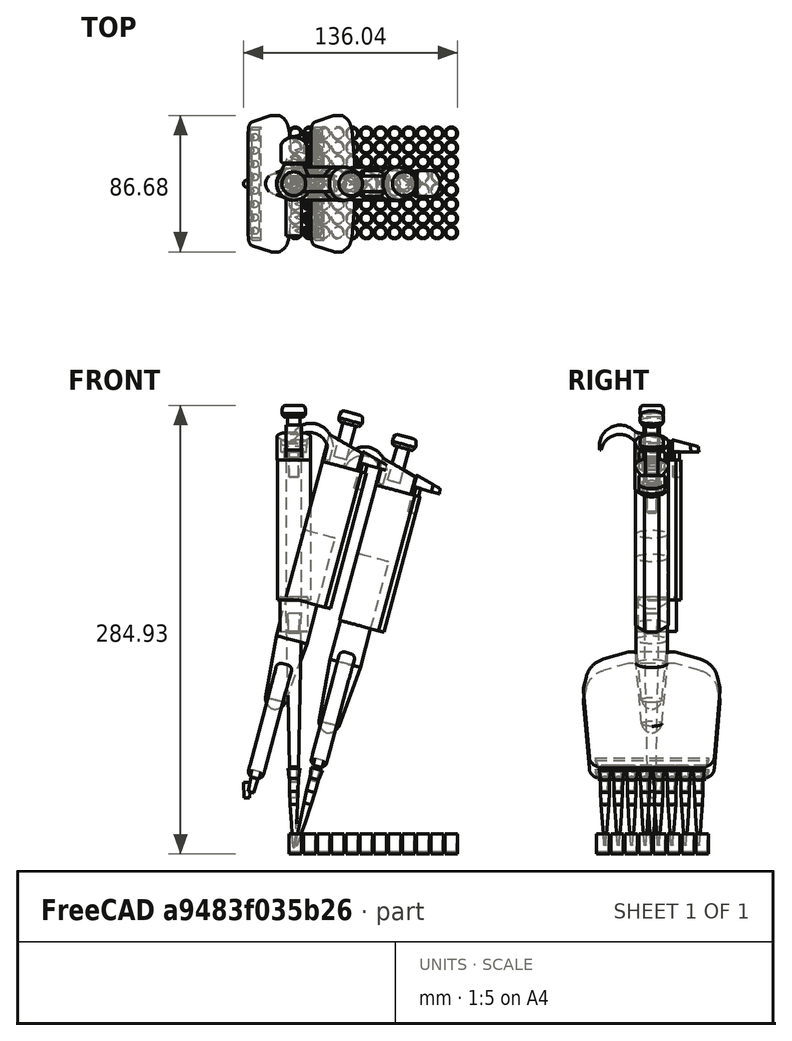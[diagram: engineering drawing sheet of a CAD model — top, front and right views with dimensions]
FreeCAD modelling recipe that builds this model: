
FCSTD DOCUMENT  (FreeCAD 0.20R29410 (Git))
Label: Pipettes
License: All rights reserved
LicenseURL: http://en.wikipedia.org/wiki/All_rights_reserved
objects: Sketcher::SketchObject×37, PartDesign::Body×30, PartDesign::Pad×14, Part::Compound×13, PartDesign::Revolution×9, Part::FeaturePython×7, PartDesign::AdditiveLoft×7, TechDraw::DrawViewPart×7, PartDesign::ShapeBinder×6, PartDesign::Plane×6, Part::Thickness×3, Image::ImagePlane×2, Part::Fillet×2, TechDraw::DrawSVGTemplate×2, TechDraw::DrawPage×2, Part::Cylinder×1, Part::Cut×1, App::Part×1
note: 160 computed .brp shape members not serialized (recipe doc carries the construction recipe); baked Part::Feature solids carry a one-line shape summary decoded from their .brp

FEATURE [Image::ImagePlane] ImagePlane
  Placement = pos=(-11,0,28) rot=(-1,0,0;4.71239rad)
  XSize = 251.23
  YSize = 373.42
FEATURE [Part::Thickness] Thickness001  label="2-200 tip"
  Intersection = false
  Join = 0
  Mode = 0
  Placement = pos=(0,0,-137) rot=(0,0,1;0rad)
  SelfIntersection = false
  Value = 0.1
FEATURE [Part::FeaturePython] Array  label="Array of tips"  # Draft array (typed FeaturePython)
  AlwaysSyncPlacement = false
  Angle = 360
  ArrayType = 0
  Axis = (0,0,1)
  Base = -> Thickness001
  Center = (0,0,0)
  Count = 8
  ExpandArray = false
  Fuse = false
  IntervalAxis = (0,0,0)
  IntervalX = (8.5,0,0)
  IntervalY = (0,100,0)
  IntervalZ = (0,0,100)
  NumberCircles = 3
  NumberPolar = 5
  NumberX = 8
  NumberY = 1
  NumberZ = 1
  Placement = pos=(-29.75,0,-11) rot=(0,0,1;0rad)
  PlacementList = 8 placements: arithmetic series from (0,0,-137) step (8.5,0,0) to (59.5,0,-137)
  RadialDistance = 50
  ScaleList = (8) [(1,1,1),(1,1,1),(1,1,1),(1,1,1),(1,1,1),(1,1,1),(1,1,1),(1,1,1)]
  Symmetry = 1
  TangentialDistance = 25
FEATURE [Sketcher::SketchObject] Sketch
  FullyConstrained = false
  MapMode = 5
  Placement = pos=(0,0,0) rot=(1,0,0;1.5708rad)
  Support = -> [XZ_Plane]
  sketch-geometry (18):
    g0: LineSegment StartX=39.7221 StartY=-89.5995 StartZ=0 EndX=43.3704 EndY=-45.7141 EndZ=0
    g1: LineSegment StartX=43.3704 StartY=-45.7141 StartZ=0 EndX=41.5984 EndY=-37.853 EndZ=0
    g2: LineSegment StartX=30.7067 StartY=-26.3243 StartZ=0 EndX=14.3773 EndY=-21.6547 EndZ=0
    g3: LineSegment StartX=-14.3773 StartY=-21.6547 StartZ=0 EndX=-30.7067 EndY=-26.3243 EndZ=0
    g4: LineSegment StartX=-41.5984 StartY=-37.853 StartZ=0 EndX=-43.3704 EndY=-45.7141 EndZ=0
    g5: LineSegment StartX=-43.3704 StartY=-45.7141 StartZ=0 EndX=-39.7221 EndY=-89.5995 EndZ=0
    g6: LineSegment StartX=-14.3773 StartY=-21.6547 StartZ=0 EndX=0 EndY=-21.6547 EndZ=0
    g7: LineSegment StartX=14.3773 StartY=-21.6547 StartZ=0 EndX=0 EndY=-21.6547 EndZ=0
    g8: LineSegment StartX=33.0605 StartY=-95.7303 StartZ=0 EndX=0 EndY=-95.7303 EndZ=0
    g9: LineSegment StartX=0 StartY=-95.7303 StartZ=0 EndX=-33.0605 EndY=-95.7303 EndZ=0
    g10: LineSegment StartX=43.3704 StartY=-45.7141 StartZ=0 EndX=-43.3704 EndY=-45.7141 EndZ=0
    g11: ArcOfCircle CenterX=26.4323 CenterY=-41.2717 CenterZ=0 NormalX=0 NormalY=0 NormalZ=1 AngleXU=0 Radius=15.5465 StartAngle=0.221711 EndAngle=1.29227
    g12: ArcOfCircle CenterX=-26.4323 CenterY=-41.2717 CenterZ=0 NormalX=0 NormalY=0 NormalZ=1 AngleXU=0 Radius=15.5465 StartAngle=1.84932 EndAngle=2.91988
    g13: LineSegment StartX=41.5984 StartY=-37.853 StartZ=0 EndX=-41.5984 EndY=-37.853 EndZ=0
    g14: LineSegment StartX=-30.7067 StartY=-26.3243 StartZ=0 EndX=30.7067 EndY=-26.3243 EndZ=0
    g15: ArcOfCircle CenterX=33.0605 CenterY=-89.0457 CenterZ=0 NormalX=0 NormalY=0 NormalZ=1 AngleXU=0 Radius=6.6846 StartAngle=4.71239 EndAngle=6.20025
    g16: ArcOfCircle CenterX=-33.0605 CenterY=-89.0457 CenterZ=0 NormalX=0 NormalY=0 NormalZ=1 AngleXU=0 Radius=6.6846 StartAngle=3.22453 EndAngle=4.71239
    g17: LineSegment StartX=39.7221 StartY=-89.5995 StartZ=0 EndX=-39.7221 EndY=-89.5995 EndZ=0
  constraints (36):
    c: Coincident(g1,g0)
    c: Coincident(g5,g4)
    c: Coincident(g6,g3)
    c: PointOnObject(g6,g-2)
    c: Horizontal(g6)
    c: Coincident(g7,g2)
    c: Coincident(g7,g6)
    c: Horizontal(g7)
    c: PointOnObject(g8,g-2)
    c: Horizontal(g8)
    c: Coincident(g9,g8)
    c: Horizontal(g9)
    c: Equal(g0,g5)
    c: Equal(g1,g4)
    c: Equal(g3,g2)
    c: Equal(g7,g6)
    c: Equal(g8,g9)
    c: Coincident(g10,g0)
    c: Coincident(g10,g4)
    c: Horizontal(g10)
    c: Tangent(g2,g11) = -1.5708
    c: Tangent(g1,g11) = -1.5708
    c: Tangent(g3,g12) = -1.5708
    c: Tangent(g4,g12) = -1.5708
    c: Coincident(g13,g1)
    c: Coincident(g13,g4)
    c: Horizontal(g13)
    c: Coincident(g14,g3)
    c: Coincident(g14,g2)
    c: Horizontal(g14)
    c: Tangent(g0,g15) = -1.5708
    c: Tangent(g8,g15) = 1.5708
    c: Tangent(g9,g16) = 1.5708
    c: Tangent(g5,g16) = -1.5708
    c: Coincident(g17,g0)
    c: Coincident(g17,g5)
FEATURE [PartDesign::Pad] Pad
  Direction = (0,-1,2e-16)
  Length = 10
  Length2 = 10
  Midplane = true
  Placement = pos=(0,0,0) rot=(1,0,0;1.5708rad)
  Profile = -> Sketch
  ReferenceAxis = -> Sketch [N_Axis]
  Type = 0
FEATURE [PartDesign::Body] Body
  Group = -> [Sketch,Pad]
  Origin = -> Origin
  Tip = -> Pad
FEATURE [Part::Fillet] Fillet  label="Main body"
  Base = -> Body
  Edges = 32 edges r=3: [Edge3,Edge4,Edge5,Edge6,Edge7,Edge9,Edge10,Edge12,Edge13,Edge14,Edge15,Edge16,Edge18,Edge19,Edge20,Edge21,Edge22,Edge24,Edge25,Edge27,Edge28,Edge29,Edge30,Edge31,Edge33,Edge34,Edge36,Edge37,Edge39,Edge40,Edge41,Edge42]
FEATURE [Sketcher::SketchObject] Sketch001
  FullyConstrained = false
  MapMode = 5
  Placement = pos=(0,0,0) rot=(1,0,0;1.5708rad)
  Support = -> [XZ_Plane001]
  sketch-geometry (6):
    g0: LineSegment StartX=0 StartY=-83.0877 StartZ=0 EndX=6.48261 EndY=-83.0877 EndZ=0
    g1: ArcOfCircle CenterX=-0.717331 CenterY=-81.8107 CenterZ=0 NormalX=0 NormalY=0 NormalZ=1 AngleXU=0 Radius=7.31232 StartAngle=4.81065 EndAngle=6.10764
    g2: LineSegment StartX=6.48261 StartY=-83.0877 StartZ=0 EndX=10 EndY=-43.4831 EndZ=0
    g3: LineSegment StartX=10 StartY=-43.4831 StartZ=0 EndX=10 EndY=25.9449 EndZ=0
    g4: LineSegment StartX=10 StartY=25.9449 StartZ=0 EndX=0 EndY=25.9449 EndZ=0
    g5: LineSegment StartX=0 StartY=25.9449 StartZ=0 EndX=0 EndY=-89.0877 EndZ=0
  constraints (14):
    c: PointOnObject(g0,g-2)
    c: Horizontal(g0)
    c: Coincident(g1,g0)
    c: Coincident(g2,g1)
    c: Coincident(g3,g2)
    c: Vertical(g3)
    c: Coincident(g4,g3)
    c: PointOnObject(g4,g-2)
    c: Horizontal(g4)
    c: Coincident(g5,g4)
    c: Coincident(g5,g1)
    c: Vertical(g5)
    c: DistanceY(g1,g0) = 6
    c: DistanceX(g4,g4) = 10
FEATURE [PartDesign::Revolution] Revolution
  Angle = 360
  Axis = (0,2e-16,1)
  Base = (0,0,0)
  Placement = pos=(0,0,0) rot=(1,0,0;1.5708rad)
  Profile = -> Sketch001
  ReferenceAxis = -> Sketch001 [V_Axis]
  Reversed = true
FEATURE [PartDesign::Body] Body001
  Group = -> [Sketch001,Revolution]
  Origin = -> Origin001
  Placement = pos=(0,0,38) rot=(0,0,1;0rad)
  Tip = -> Revolution
FEATURE [Sketcher::SketchObject] Sketch002
  AttachmentOffset = pos=(0,0,30) rot=(0,0,1;0rad)
  FullyConstrained = false
  MapMode = 5
  Placement = pos=(0,0,30) rot=(0,0,1;0rad)
  Support = -> [XY_Plane002]
  sketch-geometry (6):
    g0: ArcOfCircle CenterX=0 CenterY=0 CenterZ=0 NormalX=0 NormalY=0 NormalZ=1 AngleXU=0 Radius=10.5222 StartAngle=1.15093 EndAngle=5.13225
    g1: ArcOfCircle CenterX=13.606 CenterY=0 CenterZ=0 NormalX=0 NormalY=0 NormalZ=1 AngleXU=0 Radius=4.99301 StartAngle=5.04934 EndAngle=7.51703
    g2: LineSegment StartX=4.28922 StartY=-9.60826 StartZ=0 EndX=4.28922 EndY=9.60826 EndZ=0
    g3: LineSegment StartX=15.2568 StartY=4.71224 StartZ=0 EndX=4.28922 EndY=9.60826 EndZ=0
    g4: LineSegment StartX=15.2568 StartY=-4.71224 StartZ=0 EndX=4.28922 EndY=-9.60826 EndZ=0
    g5: LineSegment StartX=15.2568 StartY=-4.71224 StartZ=0 EndX=15.2568 EndY=4.71224 EndZ=0
  constraints (12):
    c: Coincident(g0,g-1)
    c: PointOnObject(g1,g-1)
    c: Coincident(g2,g0)
    c: Coincident(g2,g0)
    c: Vertical(g2)
    c: Coincident(g3,g1)
    c: Coincident(g3,g0)
    c: Coincident(g4,g1)
    c: Coincident(g4,g0)
    c: Coincident(g5,g1)
    c: Coincident(g5,g1)
    c: Vertical(g5)
FEATURE [PartDesign::Pad] Pad001
  Direction = (0,0,1)
  Length = 89
  Length2 = 10
  Profile = -> Sketch002
  ReferenceAxis = -> Sketch002 [N_Axis]
  Type = 0
FEATURE [PartDesign::Body] Body002  label="Handle down"
  Group = -> [Sketch002,Pad001]
  Origin = -> Origin002
  Placement = pos=(0,0,-10) rot=(0,0,1;0rad)
  Tip = -> Pad001
FEATURE [Sketcher::SketchObject] Sketch003
  FullyConstrained = false
  MapMode = 5
  Placement = pos=(0,0,0) rot=(1,0,0;1.5708rad)
  Support = -> [XZ_Plane003]
  sketch-geometry (6):
    g0: LineSegment StartX=0 StartY=-91.478 StartZ=0 EndX=35.9271 EndY=-91.478 EndZ=0
    g1: LineSegment StartX=35.9271 StartY=-91.478 StartZ=0 EndX=34.2632 EndY=-96.4699 EndZ=0
    g2: LineSegment StartX=34.2632 StartY=-96.4699 StartZ=0 EndX=0 EndY=-96.4699 EndZ=0
    g3: LineSegment StartX=0 StartY=-96.4699 StartZ=0 EndX=-34.2632 EndY=-96.4699 EndZ=0
    g4: LineSegment StartX=-34.2632 StartY=-96.4699 StartZ=0 EndX=-35.9271 EndY=-91.478 EndZ=0
    g5: LineSegment StartX=-35.9271 StartY=-91.478 StartZ=0 EndX=0 EndY=-91.478 EndZ=0
  constraints (14):
    c: PointOnObject(g0,g-2)
    c: Horizontal(g0)
    c: Coincident(g1,g0)
    c: Coincident(g2,g1)
    c: PointOnObject(g2,g-2)
    c: Horizontal(g2)
    c: Coincident(g3,g2)
    c: Horizontal(g3)
    c: Coincident(g4,g3)
    c: Coincident(g5,g4)
    c: Coincident(g5,g0)
    c: Horizontal(g5)
    c: Equal(g3,g2)
    c: Equal(g5,g0)
FEATURE [PartDesign::Pad] Pad002
  Direction = (0,-1,2e-16)
  Length = 6
  Length2 = 10
  Midplane = true
  Placement = pos=(0,0,0) rot=(1,0,0;1.5708rad)
  Profile = -> Sketch003
  ReferenceAxis = -> Sketch003 [N_Axis]
  Type = 0
FEATURE [PartDesign::Body] Body003  label="Tips holders intermediat"
  Group = -> [Sketch003,Pad002]
  Origin = -> Origin003
  Tip = -> Pad002
FEATURE [Sketcher::SketchObject] Sketch004
  FullyConstrained = false
  MapMode = 5
  Placement = pos=(0,0,0) rot=(1,0,0;1.5708rad)
  Support = -> [XZ_Plane004]
  sketch-geometry (4):
    g0: LineSegment StartX=0 StartY=-105.635 StartZ=0 EndX=1.73982 EndY=-105.635 EndZ=0
    g1: LineSegment StartX=1.73982 StartY=-105.635 StartZ=0 EndX=2.23827 EndY=-95.7656 EndZ=0
    g2: LineSegment StartX=2.23827 StartY=-95.7656 StartZ=0 EndX=0 EndY=-95.7656 EndZ=0
    g3: LineSegment StartX=0 StartY=-105.635 StartZ=0 EndX=0 EndY=-95.7656 EndZ=0
  constraints (8):
    c: PointOnObject(g0,g-2)
    c: Coincident(g1,g0)
    c: Coincident(g2,g1)
    c: PointOnObject(g2,g-2)
    c: Horizontal(g2)
    c: Coincident(g3,g0)
    c: Coincident(g3,g2)
    c: Horizontal(g0)
FEATURE [PartDesign::Revolution] Revolution001
  Angle = 360
  Axis = (0,2e-16,1)
  Base = (0,0,0)
  Placement = pos=(0,0,0) rot=(1,0,0;1.5708rad)
  Profile = -> Sketch004
  ReferenceAxis = -> Sketch004 [V_Axis]
  Reversed = true
FEATURE [PartDesign::Body] Body004
  Group = -> [Sketch004,Revolution001]
  Origin = -> Origin004
  Placement = pos=(-29.8,0,0) rot=(0,0,1;0rad)
  Tip = -> Revolution001
FEATURE [Part::FeaturePython] Array001  label="Tips holders"  # Draft array (typed FeaturePython)
  AlwaysSyncPlacement = false
  Angle = 360
  ArrayType = 0
  Axis = (0,0,1)
  Base = -> Revolution001
  Center = (0,0,0)
  Count = 8
  ExpandArray = false
  Fuse = false
  IntervalAxis = (0,0,0)
  IntervalX = (8.5,0,0)
  IntervalY = (0,100,0)
  IntervalZ = (0,0,100)
  NumberCircles = 3
  NumberPolar = 5
  NumberX = 8
  NumberY = 1
  NumberZ = 1
  Placement = pos=(-29.9,0,0) rot=(0,0,1;0rad)
  PlacementList = 8 placements: arithmetic series from (0,0,0) step (8.5,0,0) to (59.5,0,0)
  RadialDistance = 50
  ScaleList = (8) [(1,1,1),(1,1,1),(1,1,1),(1,1,1),(1,1,1),(1,1,1),(1,1,1),(1,1,1)]
  Symmetry = 1
  TangentialDistance = 25
FEATURE [Sketcher::SketchObject] Sketch005
  FullyConstrained = false
  MapMode = 5
  Placement = pos=(0,0,0) rot=(1,0,0;1.5708rad)
  Support = -> [XZ_Plane005]
  sketch-geometry (13):
    g0: LineSegment StartX=0 StartY=126.907 StartZ=0 EndX=4.00392 EndY=126.907 EndZ=0
    g1: LineSegment StartX=4.00392 StartY=126.907 StartZ=0 EndX=4.00392 EndY=149.155 EndZ=0
    g2: LineSegment StartX=4.00392 StartY=149.155 StartZ=0 EndX=6.1092 EndY=149.155 EndZ=0
    g3: LineSegment StartX=6.1092 StartY=149.155 StartZ=0 EndX=7.56082 EndY=151.528 EndZ=0
    g4: LineSegment StartX=6.45502 StartY=156.073 StartZ=0 EndX=5.512 EndY=156.456 EndZ=0
    g5: LineSegment StartX=5.13623 StartY=156.529 StartZ=0 EndX=0 EndY=156.529 EndZ=0
    g6: ArcOfCircle CenterX=3.32106 CenterY=152.491 CenterZ=0 NormalX=0 NormalY=0 NormalZ=1 AngleXU=0 Radius=4.34777 StartAngle=5.40856 EndAngle=6.05983
    g7: LineSegment StartX=7.56082 StartY=151.528 StartZ=0 EndX=7.56082 EndY=152.922 EndZ=0
    g8: LineSegment StartX=6.79086 StartY=155.718 StartZ=0 EndX=7.38546 EndY=153.978 EndZ=0
    g9: ArcOfCircle CenterX=4.2961 CenterY=152.922 CenterZ=0 NormalX=0 NormalY=0 NormalZ=1 AngleXU=0 Radius=3.26472 StartAngle=0 EndAngle=0.329246
    g10: ArcOfCircle CenterX=6.23382 CenterY=155.528 CenterZ=0 NormalX=0 NormalY=0 NormalZ=1 AngleXU=0 Radius=0.588658 StartAngle=0.329246 EndAngle=1.18556
    g11: ArcOfCircle CenterX=5.13623 CenterY=155.529 CenterZ=0 NormalX=0 NormalY=0 NormalZ=1 AngleXU=0 Radius=1 StartAngle=1.18556 EndAngle=1.5708
    g12: LineSegment StartX=0 StartY=156.529 StartZ=0 EndX=0 EndY=126.907 EndZ=0
  constraints (22):
    c: PointOnObject(g0,g-2)
    c: Horizontal(g0)
    c: Coincident(g1,g0)
    c: Vertical(g1)
    c: Coincident(g2,g1)
    c: Horizontal(g2)
    c: Coincident(g3,g2)
    c: Horizontal(g5)
    c: Coincident(g6,g2)
    c: Coincident(g6,g3)
    c: Coincident(g7,g6)
    c: Vertical(g7)
    c: Tangent(g7,g9) = -1.5708
    c: Tangent(g8,g9) = 1.5708
    c: Tangent(g8,g10) = 1.5708
    c: Tangent(g4,g10) = -1.5708
    c: Tangent(g4,g11) = -1.5708
    c: Tangent(g5,g11) = -1.5708
    c: Coincident(g12,g5)
    c: Coincident(g12,g0)
    c: Vertical(g12)
    c: Radius(g11) = 1
FEATURE [PartDesign::Revolution] Revolution002
  Angle = 360
  Axis = (0,2e-16,1)
  Base = (0,0,0)
  Placement = pos=(0,0,0) rot=(1,0,0;1.5708rad)
  Profile = -> Sketch005
  ReferenceAxis = -> Sketch005 [V_Axis]
  Reversed = true
FEATURE [PartDesign::Body] Body005  label="Button"
  Group = -> [Sketch005,Revolution002]
  Origin = -> Origin005
  Placement = pos=(0,0,-13) rot=(0,0,1;0rad)
  Tip = -> Revolution002
FEATURE [Sketcher::SketchObject] Sketch006
  AttachmentOffset = pos=(0,0,119) rot=(0,0,1;0rad)
  FullyConstrained = false
  MapMode = 5
  Placement = pos=(0,0,119) rot=(0,0,1;0rad)
  Support = -> [XY_Plane006]
  sketch-geometry (5):
    g0: ArcOfCircle CenterX=0 CenterY=0 CenterZ=0 NormalX=0 NormalY=0 NormalZ=1 AngleXU=0 Radius=10.5554 StartAngle=1.15011 EndAngle=5.13308
    g1: LineSegment StartX=4.31068 StartY=-9.63502 StartZ=0 EndX=4.31068 EndY=9.63502 EndZ=0
    g2: LineSegment StartX=12.3594 StartY=6.03403 StartZ=0 EndX=12.3594 EndY=-5.98739 EndZ=0
    g3: LineSegment StartX=12.3594 StartY=-5.98739 StartZ=0 EndX=4.31068 EndY=-9.63502 EndZ=0
    g4: LineSegment StartX=12.3594 StartY=6.03403 StartZ=0 EndX=4.31068 EndY=9.63502 EndZ=0
  constraints (9):
    c: Coincident(g0,g-1)
    c: Coincident(g1,g0)
    c: Coincident(g1,g0)
    c: Vertical(g1)
    c: Vertical(g2)
    c: Coincident(g3,g2)
    c: Coincident(g3,g0)
    c: Coincident(g4,g2)
    c: Tangent(g4,g0) = -1.5708
FEATURE [PartDesign::ShapeBinder] CopyBox
  Placement = pos=(-11,-22,113) rot=(0,1,0;0.261799rad)
  TraceSupport = false
FEATURE [PartDesign::Plane] DatumPlane
  AttachmentOffset = pos=(0,0,13) rot=(0,0,1;0rad)
  Length = 103.574
  MapMode = 5
  Placement = pos=(-5.04716,-22,135.216) rot=(0,1,0;0.261799rad)
  ResizeMode = 0
  Support = -> [CopyBox]
  Width = 63.4273
FEATURE [Sketcher::SketchObject] Sketch007
  FullyConstrained = false
  MapMode = 5
  Placement = pos=(-5.04716,-22,135.216) rot=(0,1,0;0.261799rad)
  Support = -> [DatumPlane]
  sketch-geometry (6):
    g0: ArcOfCircle CenterX=4.89643 CenterY=22 CenterZ=0 NormalX=0 NormalY=0 NormalZ=1 AngleXU=0 Radius=10.6127 StartAngle=1.17267 EndAngle=5.11052
    g1: LineSegment StartX=4.89643 StartY=22 StartZ=0 EndX=41.871 EndY=22 EndZ=0
    g2: LineSegment StartX=18.1252 StartY=27.9493 StartZ=0 EndX=9.01089 EndY=31.7827 EndZ=0
    g3: LineSegment StartX=18.1252 StartY=15.9745 StartZ=0 EndX=9.01089 EndY=12.2173 EndZ=0
    g4: LineSegment StartX=9.01089 StartY=12.2173 StartZ=0 EndX=9.01089 EndY=31.7827 EndZ=0
    g5: LineSegment StartX=18.1252 StartY=27.9493 StartZ=0 EndX=18.1252 EndY=15.9745 EndZ=0
  constraints (11):
    c: DistanceY(g0) = 22
    c: Horizontal(g1)
    c: Coincident(g4,g3)
    c: Coincident(g4,g2)
    c: Vertical(g4)
    c: Coincident(g0,g3)
    c: Coincident(g1,g0)
    c: Vertical(g5)
    c: Tangent(g0,g2) = -1.5708
    c: Coincident(g5,g3)
    c: Coincident(g2,g5)
FEATURE [Sketcher::SketchObject] Sketch008
  FullyConstrained = false
  MapMode = 5
  Placement = pos=(0,0,0) rot=(1,0,0;1.5708rad)
  Support = -> [XZ_Plane007]
  sketch-geometry (12):
    g0: LineSegment StartX=-6.06998 StartY=126.439 StartZ=0 EndX=-32.1503 EndY=115.111 EndZ=0
    g1: LineSegment StartX=-9.74812 StartY=110.531 StartZ=0 EndX=-9.74812 EndY=125.946 EndZ=0
    g2: LineSegment StartX=-9.74812 StartY=125.946 StartZ=0 EndX=-5.84974 EndY=125.946 EndZ=0
    g3: LineSegment StartX=-9.74812 StartY=110.531 StartZ=0 EndX=-5.84974 EndY=110.531 EndZ=0
    g4: ArcOfCircle CenterX=-20.1675 CenterY=112.928 CenterZ=0 NormalX=0 NormalY=0 NormalZ=1 AngleXU=0 Radius=12.18 StartAngle=0.544381 EndAngle=2.96141
    g5: ArcOfCircle CenterX=-20.139 CenterY=117.805 CenterZ=0 NormalX=0 NormalY=0 NormalZ=1 AngleXU=0 Radius=13.2 StartAngle=0.66456 EndAngle=3.34717
    g6: LineSegment StartX=-9.74812 StartY=119.236 StartZ=0 EndX=-9.74812 EndY=110.531 EndZ=0
    g7: LineSegment StartX=-6.06998 StartY=110.648 StartZ=0 EndX=-9.74812 EndY=110.531 EndZ=0
    g8: LineSegment StartX=-6.06998 StartY=126.439 StartZ=0 EndX=-6.06998 EndY=110.648 EndZ=0
    g9: ArcOfCircle CenterX=-23.8722 CenterY=113.32 CenterZ=0 NormalX=0 NormalY=0 NormalZ=1 AngleXU=0 Radius=18.9448 StartAngle=0.349079 EndAngle=0.729456
    g10: LineSegment StartX=-6.06998 StartY=110.648 StartZ=0 EndX=-6.06998 EndY=119.799 EndZ=0
    g11: LineSegment StartX=-32.1503 StartY=115.111 StartZ=0 EndX=-33.0611 EndY=115.111 EndZ=0
  constraints (24):
    c: Vertical(g1)
    c: Coincident(g2,g1)
    c: Horizontal(g2)
    c: Coincident(g3,g1)
    c: Horizontal(g3)
    c: PointOnObject(g4,g1)
    c: Coincident(g4,g0)
    c: Coincident(g5,g1)
    c: Coincident(g6,g4)
    c: Coincident(g6,g1)
    c: Coincident(g7,g6)
    c: Radius(g5) = 13.2
    c: Radius(g4) = 12.18
    c: DistanceY(g4,g5) = 6.71
    c: Coincident(g8,g0)
    c: Coincident(g8,g7)
    c: Vertical(g8)
    c: Coincident(g9,g5)
    c: PointOnObject(g9,g8)
    c: Coincident(g10,g7)
    c: Coincident(g10,g9)
    c: Coincident(g11,g4)
    c: Coincident(g11,g5)
    c: Horizontal(g11)
FEATURE [PartDesign::Pad] Pad003
  Direction = (0,-1,2e-16)
  Length = 10
  Length2 = 10
  Midplane = true
  Placement = pos=(0,0,0) rot=(1,0,0;1.5708rad)
  Profile = -> Sketch008
  ReferenceAxis = -> Sketch008 [N_Axis]
  Type = 0
FEATURE [PartDesign::Body] Body007  label="Hook"
  Group = -> [Sketch008,Pad003]
  Origin = -> Origin007
  Tip = -> Pad003
FEATURE [PartDesign::AdditiveLoft] AdditiveLoft
  Closed = false
  Profile = -> Sketch006
  Ruled = false
  Sections = -> [Sketch007]
FEATURE [PartDesign::Body] Body006  label="Handle up"
  Group = -> [Sketch006,DatumPlane,CopyBox,Sketch007,AdditiveLoft]
  Origin = -> Origin006
  Placement = pos=(0,0,-10) rot=(0,0,1;0rad)
  Tip = -> AdditiveLoft
FEATURE [Sketcher::SketchObject] Sketch010  label="Sketch down"
  AttachmentOffset = pos=(0,0,134) rot=(0,0,1;0rad)
  FullyConstrained = false
  MapMode = 5
  Placement = pos=(0,0,134) rot=(0,0,1;0rad)
  Support = -> [XY_Plane008]
  sketch-geometry (11):
    g0: ArcOfCircle CenterX=0 CenterY=0 CenterZ=0 NormalX=0 NormalY=0 NormalZ=1 AngleXU=0 Radius=10.432 StartAngle=1.15238 EndAngle=5.13081
    g1: LineSegment StartX=4.2387 StartY=-9.53202 StartZ=0 EndX=4.2387 EndY=9.53202 EndZ=0
    g2: LineSegment StartX=13.0386 StartY=-5.6648 StartZ=0 EndX=4.2387 EndY=-9.53202 EndZ=0
    g3: LineSegment StartX=13.0386 StartY=5.61889 StartZ=0 EndX=4.2387 EndY=9.53202 EndZ=0
    g4: LineSegment StartX=14.8575 StartY=8.17194 StartZ=0 EndX=24.8171 EndY=8.17194 EndZ=0
    g5: LineSegment StartX=14.8575 StartY=-8.17194 StartZ=0 EndX=24.8171 EndY=-8.17194 EndZ=0
    g6: ArcOfCircle CenterX=20.7229 CenterY=0 CenterZ=0 NormalX=0 NormalY=0 NormalZ=1 AngleXU=0 Radius=9.14017 StartAngle=5.17684 EndAngle=7.38953
    g7: LineSegment StartX=13.0386 StartY=6.353 StartZ=0 EndX=13.0386 EndY=-6.353 EndZ=0
    g8: ArcOfCircle CenterX=14.8575 CenterY=6.353 CenterZ=0 NormalX=0 NormalY=0 NormalZ=1 AngleXU=0 Radius=1.81894 StartAngle=1.5708 EndAngle=3.14159
    g9: ArcOfCircle CenterX=14.8575 CenterY=-6.353 CenterZ=0 NormalX=0 NormalY=0 NormalZ=1 AngleXU=0 Radius=1.81894 StartAngle=3.14159 EndAngle=4.71239
    g10: LineSegment StartX=13.0386 StartY=-6.353 StartZ=0 EndX=13.0386 EndY=6.353 EndZ=0
  constraints (22):
    c: Coincident(g0,g-1)
    c: Coincident(g1,g0)
    c: Coincident(g1,g0)
    c: Vertical(g1)
    c: Coincident(g2,g0)
    c: Tangent(g3,g0) = -1.5708
    c: Horizontal(g4)
    c: Horizontal(g5)
    c: Equal(g4,g5)
    c: Coincident(g6,g4)
    c: Coincident(g6,g5)
    c: PointOnObject(g6,g-1)
    c: Vertical(g7)
    c: PointOnObject(g2,g7)
    c: PointOnObject(g3,g7)
    c: Tangent(g4,g8) = 1.5708
    c: Tangent(g7,g8) = -1.5708
    c: Tangent(g5,g9) = -1.5708
    c: Tangent(g7,g9) = -1.5708
    c: Equal(g9,g8)
    c: Coincident(g10,g9)
    c: Coincident(g10,g8)
FEATURE [PartDesign::ShapeBinder] CopyBox001
  Placement = pos=(-11,-22,113) rot=(0,1,0;0.261799rad)
  TraceSupport = false
FEATURE [PartDesign::Plane] DatumPlane001
  AttachmentOffset = pos=(0,0,24) rot=(0,0,1;0rad)
  Length = 109.979
  MapMode = 5
  Placement = pos=(-2.20015,-22,145.841) rot=(0,1,0;0.261799rad)
  ResizeMode = 0
  Support = -> [CopyBox001]
  Width = 63.8647
FEATURE [Sketcher::SketchObject] Sketch009  label="Sketch up"
  FullyConstrained = false
  MapMode = 5
  Placement = pos=(-2.20015,-22,145.841) rot=(0,1,0;0.261799rad)
  Support = -> [DatumPlane001]
  sketch-geometry (13):
    g0: ArcOfCircle CenterX=4.50884 CenterY=22 CenterZ=0 NormalX=0 NormalY=0 NormalZ=1 AngleXU=0 Radius=10.4954 StartAngle=1.10018 EndAngle=5.183
    g1: LineSegment StartX=4.50884 StartY=22 StartZ=0 EndX=41.871 EndY=22 EndZ=0
    g2: LineSegment StartX=15.8862 StartY=27.9874 StartZ=0 EndX=9.26778 EndY=31.3544 EndZ=0
    g3: LineSegment StartX=15.8862 StartY=15.9218 StartZ=0 EndX=9.26778 EndY=12.6456 EndZ=0
    g4: LineSegment StartX=9.26778 StartY=12.6456 StartZ=0 EndX=9.26778 EndY=31.3544 EndZ=0
    g5: LineSegment StartX=15.8862 StartY=27.9874 StartZ=0 EndX=15.8862 EndY=15.9218 EndZ=0
    g6: LineSegment StartX=17.5392 StartY=13.7739 StartZ=0 EndX=27.6466 EndY=13.7739 EndZ=0
    g7: LineSegment StartX=17.5392 StartY=30.2261 StartZ=0 EndX=27.6466 EndY=30.2261 EndZ=0
    g8: ArcOfCircle CenterX=23.8665 CenterY=22 CenterZ=0 NormalX=0 NormalY=0 NormalZ=1 AngleXU=0 Radius=9.05303 StartAngle=5.14314 EndAngle=7.42323
    g9: LineSegment StartX=15.8862 StartY=15.4269 StartZ=0 EndX=15.8862 EndY=28.5731 EndZ=0
    g10: ArcOfCircle CenterX=17.5392 CenterY=28.5731 CenterZ=0 NormalX=0 NormalY=0 NormalZ=1 AngleXU=0 Radius=1.65299 StartAngle=1.5708 EndAngle=3.14159
    g11: ArcOfCircle CenterX=17.5392 CenterY=15.4269 CenterZ=0 NormalX=0 NormalY=0 NormalZ=1 AngleXU=0 Radius=1.65299 StartAngle=3.14159 EndAngle=4.71239
    g12: LineSegment StartX=15.8862 StartY=15.4269 StartZ=0 EndX=15.8862 EndY=28.5731 EndZ=0
  constraints (26):
    c: DistanceY(g0) = 22
    c: Horizontal(g1)
    c: Coincident(g4,g3)
    c: Coincident(g4,g2)
    c: Vertical(g4)
    c: Coincident(g0,g3)
    c: Coincident(g1,g0)
    c: Vertical(g5)
    c: Tangent(g0,g2) = -1.5708
    c: Coincident(g5,g3)
    c: Coincident(g2,g5)
    c: Horizontal(g6)
    c: Horizontal(g7)
    c: Equal(g7,g6)
    c: Coincident(g8,g7)
    c: Coincident(g8,g6)
    c: PointOnObject(g8,g1)
    c: Vertical(g9)
    c: PointOnObject(g2,g9)
    c: Tangent(g7,g10) = 1.5708
    c: Tangent(g9,g10) = 1.5708
    c: Tangent(g6,g11) = -1.5708
    c: Tangent(g9,g11) = 1.5708
    c: Coincident(g12,g11)
    c: Coincident(g12,g10)
    c: Equal(g10,g11)
FEATURE [PartDesign::AdditiveLoft] AdditiveLoft001
  Closed = false
  Profile = -> Sketch010
  Ruled = false
  Sections = -> [Sketch009]
FEATURE [PartDesign::Body] Body008  label="Handle002"
  Group = -> [Sketch010,DatumPlane001,CopyBox001,Sketch009,AdditiveLoft001]
  Origin = -> Origin008
  Placement = pos=(0,0,-10) rot=(0,0,1;0rad)
  Tip = -> AdditiveLoft001
FEATURE [Sketcher::SketchObject] Sketch011
  AttachmentOffset = pos=(0,0,108) rot=(0,0,1;0rad)
  FullyConstrained = false
  MapMode = 5
  Placement = pos=(0,0,108) rot=(0,0,1;0rad)
  Support = -> [XY_Plane009]
  sketch-geometry (5):
    g0: LineSegment StartX=13.4509 StartY=2.99279 StartZ=0 EndX=13.4509 EndY=-2.99279 EndZ=0
    g1: LineSegment StartX=13.4509 StartY=2.99279 StartZ=0 EndX=14.5401 EndY=2.99279 EndZ=0
    g2: LineSegment StartX=13.4509 StartY=-2.99279 StartZ=0 EndX=14.5401 EndY=-2.99279 EndZ=0
    g3: ArcOfCircle CenterX=14.6831 CenterY=0 CenterZ=0 NormalX=0 NormalY=0 NormalZ=1 AngleXU=0 Radius=2.99621 StartAngle=4.66462 EndAngle=7.90175
    g4: LineSegment StartX=14.5401 StartY=2.99279 StartZ=0 EndX=14.5401 EndY=-2.99279 EndZ=0
  constraints (11):
    c: Vertical(g0)
    c: Coincident(g1,g0)
    c: Horizontal(g1)
    c: Coincident(g2,g0)
    c: Horizontal(g2)
    c: Coincident(g3,g1)
    c: Coincident(g3,g2)
    c: PointOnObject(g3,g-1)
    c: Coincident(g4,g1)
    c: Coincident(g4,g2)
    c: Vertical(g4)
FEATURE [PartDesign::Pad] Pad004
  Direction = (0,0,1)
  Length = 17
  Length2 = 10
  Profile = -> Sketch011
  ReferenceAxis = -> Sketch011 [N_Axis]
  Type = 0
FEATURE [PartDesign::Body] Body009
  Group = -> [Sketch011,Pad004]
  Origin = -> Origin009
  Tip = -> Pad004
FEATURE [Part::Compound] Compound001  label="Tip disposal button"
  Links = -> [Body009,Body008]
  Placement = pos=(0,0,-10) rot=(0,0,1;0rad)
FEATURE [Part::Compound] Compound002  label="Upper part"
  Links = -> [Body007,Body006,Body005,Compound001,Body002,Body001]
FEATURE [Sketcher::SketchObject] Sketch016  label="D1"
  AttachmentOffset = pos=(0,0,11.3) rot=(0,0,1;0rad)
  FullyConstrained = true
  MapMode = 5
  Placement = pos=(0,0,11.3) rot=(0,0,1;0rad)
  Support = -> [XY_Plane011]
  sketch-geometry (1):
    g0: Circle CenterX=0 CenterY=0 CenterZ=0 NormalX=0 NormalY=0 NormalZ=1 AngleXU=0 Radius=3.5
  constraints (2):
    c: Coincident(g0,g-1)
    c: Diameter(g0) = 7
FEATURE [Sketcher::SketchObject] Sketch017  label="D2"
  FullyConstrained = true
  MapMode = 5
  Support = -> [XY_Plane011]
  sketch-geometry (1):
    g0: Circle CenterX=0 CenterY=0 CenterZ=0 NormalX=0 NormalY=0 NormalZ=1 AngleXU=0 Radius=3.4
  constraints (2):
    c: Coincident(g0,g-1)
    c: Diameter(g0) = 6.8
FEATURE [PartDesign::AdditiveLoft] AdditiveLoft005
  Closed = false
  Profile = -> Sketch017
  Ruled = false
  Sections = -> [Sketch016]
FEATURE [PartDesign::Body] Body011  label="Well from technical data"
  Group = -> [Sketch016,Sketch017,AdditiveLoft005]
  Origin = -> Origin011
  Tip = -> AdditiveLoft005
FEATURE [Part::FeaturePython] Array008  label="Well hole array TD"  # Draft array (typed FeaturePython)
  AlwaysSyncPlacement = false
  Angle = 360
  ArrayType = 0
  Axis = (0,0,1)
  Base = -> Body011
  Center = (0,0,0)
  Count = 96
  ExpandArray = false
  Fuse = false
  IntervalAxis = (0,0,0)
  IntervalX = (9,0,0)
  IntervalY = (0,9,0)
  IntervalZ = (0,0,100)
  NumberCircles = 3
  NumberPolar = 5
  NumberX = 12
  NumberY = 8
  NumberZ = 1
  PlacementList = 96 placements: [(0,0,0),(0,9,0),(0,18,0),(0,27,0),(0,36,0),(0,45,0),(0,54,0),(0,63,0),(9,0,0),(9,9,0),(9,18,0),(9,27,0),(9,36,0),(9,45,0),(9,54,0),(9,63,0),(18,0,0),(18,9,0),(18,18,0),(18,27,0),(18,36,0),(18,45,0),(18,54,0),(18,63,0),(27,0,0),(27,9,0),(27,18,0),(27,27,0),(27,36,0),(27,45,0),(27,54,0),(27,63,0),(36,0,0),(36,9,0),(36,18,0),(36,27,0),(36,36,0),(36,45,0),(36,54,0),(36,63,0),(45,0,0),(45,9,0),+54 more]
  RadialDistance = 50
  ScaleList = (96) [(1,1,1),(1,1,1),(1,1,1),(1,1,1),(1,1,1),(1,1,1),(1,1,1),(1,1,1),(1,1,1),(1,1,1),(1,1,1),(1,1,1),(1,1,1),(1,1,1),(1,1,1),(1,1,1),(1,1,1),(1,1,1),+78 more]
  Symmetry = 1
  TangentialDistance = 25
FEATURE [Part::Cylinder] Cylinder002  label="Well walls"
  Angle = 360
  AttacherType = Attacher::AttachEngine3D
  FirstAngle = 0
  Height = 12.7
  Placement = pos=(0,0,-1.4) rot=(0,0,1;0rad)
  Radius = 4
  SecondAngle = 0
FEATURE [Part::FeaturePython] Array009  label="Well walls array"  # Draft array (typed FeaturePython)
  AlwaysSyncPlacement = false
  Angle = 360
  ArrayType = 0
  Axis = (0,0,1)
  Base = -> Cylinder002
  Center = (0,0,0)
  Count = 96
  ExpandArray = false
  Fuse = false
  IntervalAxis = (0,0,0)
  IntervalX = (9,0,0)
  IntervalY = (0,9,0)
  IntervalZ = (0,0,100)
  NumberCircles = 3
  NumberPolar = 5
  NumberX = 12
  NumberY = 8
  NumberZ = 1
  PlacementList = 96 placements: [(0,0,-1.4),(0,9,-1.4),(0,18,-1.4),(0,27,-1.4),(0,36,-1.4),(0,45,-1.4),(0,54,-1.4),(0,63,-1.4),(9,0,-1.4),(9,9,-1.4),(9,18,-1.4),(9,27,-1.4),(9,36,-1.4),(9,45,-1.4),(9,54,-1.4),(9,63,-1.4),(18,0,-1.4),(18,9,-1.4),(18,18,-1.4),(18,27,-1.4),(18,36,-1.4),(18,45,-1.4),(18,54,-1.4),(18,63,-1.4),(27,0,-1.4),(27,9,-1.4),(27,18,-1.4),(27,27,-1.4),(27,36,-1.4),(27,45,-1.4),(27,54,-1.4),(27,63,-1.4),+64 more]
  RadialDistance = 50
  ScaleList = (96) [(1,1,1),(1,1,1),(1,1,1),(1,1,1),(1,1,1),(1,1,1),(1,1,1),(1,1,1),(1,1,1),(1,1,1),(1,1,1),(1,1,1),(1,1,1),(1,1,1),(1,1,1),(1,1,1),(1,1,1),(1,1,1),+78 more]
  Symmetry = 1
  TangentialDistance = 25
FEATURE [Part::Cut] Cut003  label="Wells from TD"
  Base = -> Array009
  Placement = pos=(1,-31,-140) rot=(0,0,1;0rad)
  Tool = -> Array008
FEATURE [Part::Compound] Compound  label="Bottom part"
  Links = -> [Array,Fillet,Body003,Array001]
  Placement = pos=(0,0,23) rot=(0,0,1;1.5708rad)
FEATURE [Part::Compound] Compound003  label="200 multichannel "
  Links = -> [Compound002,Compound]
  Placement = pos=(34,0,-15) rot=(0,1,0;0.261799rad)
FEATURE [Sketcher::SketchObject] Sketch018
  FullyConstrained = false
  MapMode = 5
  Placement = pos=(0,0,0) rot=(1,0,0;1.5708rad)
  Support = -> [XZ_Plane012]
  sketch-geometry (18):
    g0: LineSegment StartX=39.7221 StartY=-89.5995 StartZ=0 EndX=43.3704 EndY=-45.7141 EndZ=0
    g1: LineSegment StartX=43.3704 StartY=-45.7141 StartZ=0 EndX=41.5984 EndY=-37.853 EndZ=0
    g2: LineSegment StartX=30.7067 StartY=-26.3243 StartZ=0 EndX=14.3773 EndY=-21.6547 EndZ=0
    g3: LineSegment StartX=-14.3773 StartY=-21.6547 StartZ=0 EndX=-30.7067 EndY=-26.3243 EndZ=0
    g4: LineSegment StartX=-41.5984 StartY=-37.853 StartZ=0 EndX=-43.3704 EndY=-45.7141 EndZ=0
    g5: LineSegment StartX=-43.3704 StartY=-45.7141 StartZ=0 EndX=-39.7221 EndY=-89.5995 EndZ=0
    g6: LineSegment StartX=-14.3773 StartY=-21.6547 StartZ=0 EndX=0 EndY=-21.6547 EndZ=0
    g7: LineSegment StartX=14.3773 StartY=-21.6547 StartZ=0 EndX=0 EndY=-21.6547 EndZ=0
    g8: LineSegment StartX=33.0605 StartY=-95.7303 StartZ=0 EndX=0 EndY=-95.7303 EndZ=0
    g9: LineSegment StartX=0 StartY=-95.7303 StartZ=0 EndX=-33.0605 EndY=-95.7303 EndZ=0
    g10: LineSegment StartX=43.3704 StartY=-45.7141 StartZ=0 EndX=-43.3704 EndY=-45.7141 EndZ=0
    g11: ArcOfCircle CenterX=26.4323 CenterY=-41.2717 CenterZ=0 NormalX=0 NormalY=0 NormalZ=1 AngleXU=0 Radius=15.5465 StartAngle=0.221711 EndAngle=1.29227
    g12: ArcOfCircle CenterX=-26.4323 CenterY=-41.2717 CenterZ=0 NormalX=0 NormalY=0 NormalZ=1 AngleXU=0 Radius=15.5465 StartAngle=1.84932 EndAngle=2.91988
    g13: LineSegment StartX=41.5984 StartY=-37.853 StartZ=0 EndX=-41.5984 EndY=-37.853 EndZ=0
    g14: LineSegment StartX=-30.7067 StartY=-26.3243 StartZ=0 EndX=30.7067 EndY=-26.3243 EndZ=0
    g15: ArcOfCircle CenterX=33.0605 CenterY=-89.0457 CenterZ=0 NormalX=0 NormalY=0 NormalZ=1 AngleXU=0 Radius=6.6846 StartAngle=4.71239 EndAngle=6.20025
    g16: ArcOfCircle CenterX=-33.0605 CenterY=-89.0457 CenterZ=0 NormalX=0 NormalY=0 NormalZ=1 AngleXU=0 Radius=6.6846 StartAngle=3.22453 EndAngle=4.71239
    g17: LineSegment StartX=39.7221 StartY=-89.5995 StartZ=0 EndX=-39.7221 EndY=-89.5995 EndZ=0
  constraints (36):
    c: Coincident(g1,g0)
    c: Coincident(g5,g4)
    c: Coincident(g6,g3)
    c: PointOnObject(g6,g-2)
    c: Horizontal(g6)
    c: Coincident(g7,g2)
    c: Coincident(g7,g6)
    c: Horizontal(g7)
    c: PointOnObject(g8,g-2)
    c: Horizontal(g8)
    c: Coincident(g9,g8)
    c: Horizontal(g9)
    c: Equal(g0,g5)
    c: Equal(g1,g4)
    c: Equal(g3,g2)
    c: Equal(g7,g6)
    c: Equal(g8,g9)
    c: Coincident(g10,g0)
    c: Coincident(g10,g4)
    c: Horizontal(g10)
    c: Tangent(g2,g11) = -1.5708
    c: Tangent(g1,g11) = -1.5708
    c: Tangent(g3,g12) = -1.5708
    c: Tangent(g4,g12) = -1.5708
    c: Coincident(g13,g1)
    c: Coincident(g13,g4)
    c: Horizontal(g13)
    c: Coincident(g14,g3)
    c: Coincident(g14,g2)
    c: Horizontal(g14)
    c: Tangent(g0,g15) = -1.5708
    c: Tangent(g8,g15) = 1.5708
    c: Tangent(g9,g16) = 1.5708
    c: Tangent(g5,g16) = -1.5708
    c: Coincident(g17,g0)
    c: Coincident(g17,g5)
FEATURE [Part::Thickness] Thickness002  label="2-200 tip001"
  Intersection = false
  Join = 0
  Mode = 0
  Placement = pos=(0,0,-137) rot=(0,0,1;0rad)
  SelfIntersection = false
  Value = 0.1
FEATURE [Part::FeaturePython] Array011  label="Array of tips001"  # Draft array (typed FeaturePython)
  AlwaysSyncPlacement = false
  Angle = 360
  ArrayType = 0
  Axis = (0,0,1)
  Base = -> Thickness002
  Center = (0,0,0)
  Count = 8
  ExpandArray = false
  Fuse = false
  IntervalAxis = (0,0,0)
  IntervalX = (8.5,0,0)
  IntervalY = (0,100,0)
  IntervalZ = (0,0,100)
  NumberCircles = 3
  NumberPolar = 5
  NumberX = 8
  NumberY = 1
  NumberZ = 1
  Placement = pos=(-29.75,0,-11) rot=(0,0,1;0rad)
  PlacementList = 8 placements: arithmetic series from (0,0,-137) step (8.5,0,0) to (59.5,0,-137)
  RadialDistance = 50
  ScaleList = (8) [(1,1,1),(1,1,1),(1,1,1),(1,1,1),(1,1,1),(1,1,1),(1,1,1),(1,1,1)]
  Symmetry = 1
  TangentialDistance = 25
FEATURE [PartDesign::Pad] Pad008
  Direction = (0,-1,2e-16)
  Length = 10
  Length2 = 10
  Midplane = true
  Placement = pos=(0,0,0) rot=(1,0,0;1.5708rad)
  Profile = -> Sketch018
  ReferenceAxis = -> Sketch018 [N_Axis]
  Type = 0
FEATURE [PartDesign::Body] Body012
  Group = -> [Sketch018,Pad008]
  Origin = -> Origin012
  Tip = -> Pad008
FEATURE [Part::Fillet] Fillet001  label="Main body001"
  Base = -> Body012
  Edges = 32 edges r=3: [Edge3,Edge4,Edge5,Edge6,Edge7,Edge9,Edge10,Edge12,Edge13,Edge14,Edge15,Edge16,Edge18,Edge19,Edge20,Edge21,Edge22,Edge24,Edge25,Edge27,Edge28,Edge29,Edge30,Edge31,Edge33,Edge34,Edge36,Edge37,Edge39,Edge40,Edge41,Edge42]
FEATURE [Sketcher::SketchObject] Sketch019
  AttachmentOffset = pos=(0,0,30) rot=(0,0,1;0rad)
  FullyConstrained = false
  MapMode = 5
  Placement = pos=(0,0,30) rot=(0,0,1;0rad)
  Support = -> [XY_Plane013]
  sketch-geometry (6):
    g0: ArcOfCircle CenterX=0 CenterY=0 CenterZ=0 NormalX=0 NormalY=0 NormalZ=1 AngleXU=0 Radius=10.5222 StartAngle=1.15093 EndAngle=5.13225
    g1: ArcOfCircle CenterX=13.606 CenterY=0 CenterZ=0 NormalX=0 NormalY=0 NormalZ=1 AngleXU=0 Radius=4.99301 StartAngle=5.04934 EndAngle=7.51703
    g2: LineSegment StartX=4.28922 StartY=-9.60826 StartZ=0 EndX=4.28922 EndY=9.60826 EndZ=0
    g3: LineSegment StartX=15.2568 StartY=4.71224 StartZ=0 EndX=4.28922 EndY=9.60826 EndZ=0
    g4: LineSegment StartX=15.2568 StartY=-4.71224 StartZ=0 EndX=4.28922 EndY=-9.60826 EndZ=0
    g5: LineSegment StartX=15.2568 StartY=-4.71224 StartZ=0 EndX=15.2568 EndY=4.71224 EndZ=0
  constraints (12):
    c: Coincident(g0,g-1)
    c: PointOnObject(g1,g-1)
    c: Coincident(g2,g0)
    c: Coincident(g2,g0)
    c: Vertical(g2)
    c: Coincident(g3,g1)
    c: Coincident(g3,g0)
    c: Coincident(g4,g1)
    c: Coincident(g4,g0)
    c: Coincident(g5,g1)
    c: Coincident(g5,g1)
    c: Vertical(g5)
FEATURE [PartDesign::Pad] Pad007
  Direction = (0,0,1)
  Length = 89
  Length2 = 10
  Profile = -> Sketch019
  ReferenceAxis = -> Sketch019 [N_Axis]
  Type = 0
FEATURE [Sketcher::SketchObject] Sketch020
  FullyConstrained = false
  MapMode = 5
  Placement = pos=(0,0,0) rot=(1,0,0;1.5708rad)
  Support = -> [XZ_Plane014]
  sketch-geometry (6):
    g0: LineSegment StartX=0 StartY=-91.478 StartZ=0 EndX=35.9271 EndY=-91.478 EndZ=0
    g1: LineSegment StartX=35.9271 StartY=-91.478 StartZ=0 EndX=34.2632 EndY=-96.4699 EndZ=0
    g2: LineSegment StartX=34.2632 StartY=-96.4699 StartZ=0 EndX=0 EndY=-96.4699 EndZ=0
    g3: LineSegment StartX=0 StartY=-96.4699 StartZ=0 EndX=-34.2632 EndY=-96.4699 EndZ=0
    g4: LineSegment StartX=-34.2632 StartY=-96.4699 StartZ=0 EndX=-35.9271 EndY=-91.478 EndZ=0
    g5: LineSegment StartX=-35.9271 StartY=-91.478 StartZ=0 EndX=0 EndY=-91.478 EndZ=0
  constraints (14):
    c: PointOnObject(g0,g-2)
    c: Horizontal(g0)
    c: Coincident(g1,g0)
    c: Coincident(g2,g1)
    c: PointOnObject(g2,g-2)
    c: Horizontal(g2)
    c: Coincident(g3,g2)
    c: Horizontal(g3)
    c: Coincident(g4,g3)
    c: Coincident(g5,g4)
    c: Coincident(g5,g0)
    c: Horizontal(g5)
    c: Equal(g3,g2)
    c: Equal(g5,g0)
FEATURE [PartDesign::Pad] Pad009
  Direction = (0,-1,2e-16)
  Length = 6
  Length2 = 10
  Midplane = true
  Placement = pos=(0,0,0) rot=(1,0,0;1.5708rad)
  Profile = -> Sketch020
  ReferenceAxis = -> Sketch020 [N_Axis]
  Type = 0
FEATURE [PartDesign::Body] Body013  label="Tips holders intermediat001"
  Group = -> [Sketch020,Pad009]
  Origin = -> Origin015
  Tip = -> Pad009
FEATURE [Sketcher::SketchObject] Sketch021
  FullyConstrained = false
  MapMode = 5
  Placement = pos=(0,0,0) rot=(1,0,0;1.5708rad)
  Support = -> [XZ_Plane018]
  sketch-geometry (12):
    g0: LineSegment StartX=-6.06998 StartY=126.439 StartZ=0 EndX=-32.1503 EndY=115.111 EndZ=0
    g1: LineSegment StartX=-9.74812 StartY=110.531 StartZ=0 EndX=-9.74812 EndY=125.946 EndZ=0
    g2: LineSegment StartX=-9.74812 StartY=125.946 StartZ=0 EndX=-5.84974 EndY=125.946 EndZ=0
    g3: LineSegment StartX=-9.74812 StartY=110.531 StartZ=0 EndX=-5.84974 EndY=110.531 EndZ=0
    g4: ArcOfCircle CenterX=-20.1675 CenterY=112.928 CenterZ=0 NormalX=0 NormalY=0 NormalZ=1 AngleXU=0 Radius=12.18 StartAngle=0.544381 EndAngle=2.96141
    g5: ArcOfCircle CenterX=-20.139 CenterY=117.805 CenterZ=0 NormalX=0 NormalY=0 NormalZ=1 AngleXU=0 Radius=13.2 StartAngle=0.66456 EndAngle=3.34717
    g6: LineSegment StartX=-9.74812 StartY=119.236 StartZ=0 EndX=-9.74812 EndY=110.531 EndZ=0
    g7: LineSegment StartX=-6.06998 StartY=110.648 StartZ=0 EndX=-9.74812 EndY=110.531 EndZ=0
    g8: LineSegment StartX=-6.06998 StartY=126.439 StartZ=0 EndX=-6.06998 EndY=110.648 EndZ=0
    g9: ArcOfCircle CenterX=-23.8722 CenterY=113.32 CenterZ=0 NormalX=0 NormalY=0 NormalZ=1 AngleXU=0 Radius=18.9448 StartAngle=0.349079 EndAngle=0.729456
    g10: LineSegment StartX=-6.06998 StartY=110.648 StartZ=0 EndX=-6.06998 EndY=119.799 EndZ=0
    g11: LineSegment StartX=-32.1503 StartY=115.111 StartZ=0 EndX=-33.0611 EndY=115.111 EndZ=0
  constraints (24):
    c: Vertical(g1)
    c: Coincident(g2,g1)
    c: Horizontal(g2)
    c: Coincident(g3,g1)
    c: Horizontal(g3)
    c: PointOnObject(g4,g1)
    c: Coincident(g4,g0)
    c: Coincident(g5,g1)
    c: Coincident(g6,g4)
    c: Coincident(g6,g1)
    c: Coincident(g7,g6)
    c: Radius(g5) = 13.2
    c: Radius(g4) = 12.18
    c: DistanceY(g4,g5) = 6.71
    c: Coincident(g8,g0)
    c: Coincident(g8,g7)
    c: Vertical(g8)
    c: Coincident(g9,g5)
    c: PointOnObject(g9,g8)
    c: Coincident(g10,g7)
    c: Coincident(g10,g9)
    c: Coincident(g11,g4)
    c: Coincident(g11,g5)
    c: Horizontal(g11)
FEATURE [PartDesign::Pad] Pad005
  Direction = (0,-1,2e-16)
  Length = 10
  Length2 = 10
  Midplane = true
  Placement = pos=(0,0,0) rot=(1,0,0;1.5708rad)
  Profile = -> Sketch021
  ReferenceAxis = -> Sketch021 [N_Axis]
  Type = 0
FEATURE [PartDesign::Body] Body014  label="Hook001"
  Group = -> [Sketch021,Pad005]
  Origin = -> Origin019
  Tip = -> Pad005
FEATURE [Sketcher::SketchObject] Sketch023
  FullyConstrained = false
  MapMode = 5
  Placement = pos=(0,0,0) rot=(1,0,0;1.5708rad)
  Support = -> [XZ_Plane015]
  sketch-geometry (13):
    g0: LineSegment StartX=0 StartY=126.907 StartZ=0 EndX=4.00392 EndY=126.907 EndZ=0
    g1: LineSegment StartX=4.00392 StartY=126.907 StartZ=0 EndX=4.00392 EndY=149.155 EndZ=0
    g2: LineSegment StartX=4.00392 StartY=149.155 StartZ=0 EndX=6.1092 EndY=149.155 EndZ=0
    g3: LineSegment StartX=6.1092 StartY=149.155 StartZ=0 EndX=7.56082 EndY=151.528 EndZ=0
    g4: LineSegment StartX=6.45502 StartY=156.073 StartZ=0 EndX=5.512 EndY=156.456 EndZ=0
    g5: LineSegment StartX=5.13623 StartY=156.529 StartZ=0 EndX=0 EndY=156.529 EndZ=0
    g6: ArcOfCircle CenterX=3.32106 CenterY=152.491 CenterZ=0 NormalX=0 NormalY=0 NormalZ=1 AngleXU=0 Radius=4.34777 StartAngle=5.40856 EndAngle=6.05983
    g7: LineSegment StartX=7.56082 StartY=151.528 StartZ=0 EndX=7.56082 EndY=152.922 EndZ=0
    g8: LineSegment StartX=6.79086 StartY=155.718 StartZ=0 EndX=7.38546 EndY=153.978 EndZ=0
    g9: ArcOfCircle CenterX=4.2961 CenterY=152.922 CenterZ=0 NormalX=0 NormalY=0 NormalZ=1 AngleXU=0 Radius=3.26472 StartAngle=0 EndAngle=0.329246
    g10: ArcOfCircle CenterX=6.23382 CenterY=155.528 CenterZ=0 NormalX=0 NormalY=0 NormalZ=1 AngleXU=0 Radius=0.588658 StartAngle=0.329246 EndAngle=1.18556
    g11: ArcOfCircle CenterX=5.13623 CenterY=155.529 CenterZ=0 NormalX=0 NormalY=0 NormalZ=1 AngleXU=0 Radius=1 StartAngle=1.18556 EndAngle=1.5708
    g12: LineSegment StartX=0 StartY=156.529 StartZ=0 EndX=0 EndY=126.907 EndZ=0
  constraints (22):
    c: PointOnObject(g0,g-2)
    c: Horizontal(g0)
    c: Coincident(g1,g0)
    c: Vertical(g1)
    c: Coincident(g2,g1)
    c: Horizontal(g2)
    c: Coincident(g3,g2)
    c: Horizontal(g5)
    c: Coincident(g6,g2)
    c: Coincident(g6,g3)
    c: Coincident(g7,g6)
    c: Vertical(g7)
    c: Tangent(g7,g9) = -1.5708
    c: Tangent(g8,g9) = 1.5708
    c: Tangent(g8,g10) = 1.5708
    c: Tangent(g4,g10) = -1.5708
    c: Tangent(g4,g11) = -1.5708
    c: Tangent(g5,g11) = -1.5708
    c: Coincident(g12,g5)
    c: Coincident(g12,g0)
    c: Vertical(g12)
    c: Radius(g11) = 1
FEATURE [PartDesign::Revolution] Revolution003
  Angle = 360
  Axis = (0,2e-16,1)
  Base = (0,0,0)
  Placement = pos=(0,0,0) rot=(1,0,0;1.5708rad)
  Profile = -> Sketch023
  ReferenceAxis = -> Sketch023 [V_Axis]
  Reversed = true
FEATURE [Sketcher::SketchObject] Sketch025
  FullyConstrained = false
  MapMode = 5
  Placement = pos=(0,0,0) rot=(1,0,0;1.5708rad)
  Support = -> [XZ_Plane016]
  sketch-geometry (6):
    g0: LineSegment StartX=0 StartY=-83.0877 StartZ=0 EndX=6.48261 EndY=-83.0877 EndZ=0
    g1: ArcOfCircle CenterX=-0.717331 CenterY=-81.8107 CenterZ=0 NormalX=0 NormalY=0 NormalZ=1 AngleXU=0 Radius=7.31232 StartAngle=4.81065 EndAngle=6.10764
    g2: LineSegment StartX=6.48261 StartY=-83.0877 StartZ=0 EndX=10 EndY=-43.4831 EndZ=0
    g3: LineSegment StartX=10 StartY=-43.4831 StartZ=0 EndX=10 EndY=25.9449 EndZ=0
    g4: LineSegment StartX=10 StartY=25.9449 StartZ=0 EndX=0 EndY=25.9449 EndZ=0
    g5: LineSegment StartX=0 StartY=25.9449 StartZ=0 EndX=0 EndY=-89.0877 EndZ=0
  constraints (14):
    c: PointOnObject(g0,g-2)
    c: Horizontal(g0)
    c: Coincident(g1,g0)
    c: Coincident(g2,g1)
    c: Coincident(g3,g2)
    c: Vertical(g3)
    c: Coincident(g4,g3)
    c: PointOnObject(g4,g-2)
    c: Horizontal(g4)
    c: Coincident(g5,g4)
    c: Coincident(g5,g1)
    c: Vertical(g5)
    c: DistanceY(g1,g0) = 6
    c: DistanceX(g4,g4) = 10
FEATURE [PartDesign::Revolution] Revolution005
  Angle = 360
  Axis = (0,2e-16,1)
  Base = (0,0,0)
  Placement = pos=(0,0,0) rot=(1,0,0;1.5708rad)
  Profile = -> Sketch025
  ReferenceAxis = -> Sketch025 [V_Axis]
  Reversed = true
FEATURE [PartDesign::Body] Body015
  Group = -> [Sketch025,Revolution005]
  Origin = -> Origin014
  Placement = pos=(0,0,38) rot=(0,0,1;0rad)
  Tip = -> Revolution005
FEATURE [Sketcher::SketchObject] Sketch026
  AttachmentOffset = pos=(0,0,119) rot=(0,0,1;0rad)
  FullyConstrained = false
  MapMode = 5
  Placement = pos=(0,0,119) rot=(0,0,1;0rad)
  Support = -> [XY_Plane018]
  sketch-geometry (5):
    g0: ArcOfCircle CenterX=0 CenterY=0 CenterZ=0 NormalX=0 NormalY=0 NormalZ=1 AngleXU=0 Radius=10.5554 StartAngle=1.15011 EndAngle=5.13308
    g1: LineSegment StartX=4.31068 StartY=-9.63502 StartZ=0 EndX=4.31068 EndY=9.63502 EndZ=0
    g2: LineSegment StartX=12.3594 StartY=6.03403 StartZ=0 EndX=12.3594 EndY=-5.98739 EndZ=0
    g3: LineSegment StartX=12.3594 StartY=-5.98739 StartZ=0 EndX=4.31068 EndY=-9.63502 EndZ=0
    g4: LineSegment StartX=12.3594 StartY=6.03403 StartZ=0 EndX=4.31068 EndY=9.63502 EndZ=0
  constraints (9):
    c: Coincident(g0,g-1)
    c: Coincident(g1,g0)
    c: Coincident(g1,g0)
    c: Vertical(g1)
    c: Vertical(g2)
    c: Coincident(g3,g2)
    c: Coincident(g3,g0)
    c: Coincident(g4,g2)
    c: Tangent(g4,g0) = -1.5708
FEATURE [PartDesign::ShapeBinder] CopyBox002
  Placement = pos=(-11,-22,113) rot=(0,1,0;0.261799rad)
  TraceSupport = false
FEATURE [PartDesign::Plane] DatumPlane002
  AttachmentOffset = pos=(0,0,13) rot=(0,0,1;0rad)
  Length = 103.574
  MapMode = 5
  Placement = pos=(-5.04716,-22,135.216) rot=(0,1,0;0.261799rad)
  ResizeMode = 0
  Support = -> [CopyBox002]
  Width = 63.4273
FEATURE [Sketcher::SketchObject] Sketch024
  FullyConstrained = false
  MapMode = 5
  Placement = pos=(-5.04716,-22,135.216) rot=(0,1,0;0.261799rad)
  Support = -> [DatumPlane002]
  sketch-geometry (6):
    g0: ArcOfCircle CenterX=4.89643 CenterY=22 CenterZ=0 NormalX=0 NormalY=0 NormalZ=1 AngleXU=0 Radius=10.6127 StartAngle=1.17267 EndAngle=5.11052
    g1: LineSegment StartX=4.89643 StartY=22 StartZ=0 EndX=41.871 EndY=22 EndZ=0
    g2: LineSegment StartX=18.1252 StartY=27.9493 StartZ=0 EndX=9.01089 EndY=31.7827 EndZ=0
    g3: LineSegment StartX=18.1252 StartY=15.9745 StartZ=0 EndX=9.01089 EndY=12.2173 EndZ=0
    g4: LineSegment StartX=9.01089 StartY=12.2173 StartZ=0 EndX=9.01089 EndY=31.7827 EndZ=0
    g5: LineSegment StartX=18.1252 StartY=27.9493 StartZ=0 EndX=18.1252 EndY=15.9745 EndZ=0
  constraints (11):
    c: DistanceY(g0) = 22
    c: Horizontal(g1)
    c: Coincident(g4,g3)
    c: Coincident(g4,g2)
    c: Vertical(g4)
    c: Coincident(g0,g3)
    c: Coincident(g1,g0)
    c: Vertical(g5)
    c: Tangent(g0,g2) = -1.5708
    c: Coincident(g5,g3)
    c: Coincident(g2,g5)
FEATURE [PartDesign::Body] Body016  label="Handle down001"
  Group = -> [Sketch019,Pad007]
  Origin = -> Origin018
  Placement = pos=(0,0,-10) rot=(0,0,1;0rad)
  Tip = -> Pad007
FEATURE [PartDesign::AdditiveLoft] AdditiveLoft006
  Closed = false
  Profile = -> Sketch026
  Ruled = false
  Sections = -> [Sketch024]
FEATURE [PartDesign::ShapeBinder] CopyBox003
  Placement = pos=(-11,-22,113) rot=(0,1,0;0.261799rad)
  TraceSupport = false
FEATURE [PartDesign::Plane] DatumPlane003
  AttachmentOffset = pos=(0,0,24) rot=(0,0,1;0rad)
  Length = 109.979
  MapMode = 5
  Placement = pos=(-2.20015,-22,145.841) rot=(0,1,0;0.261799rad)
  ResizeMode = 0
  Support = -> [CopyBox003]
  Width = 63.8647
FEATURE [PartDesign::Body] Body019  label="Button001"
  Group = -> [Sketch023,Revolution003]
  Origin = -> Origin016
  Placement = pos=(0,0,-13) rot=(0,0,1;0rad)
  Tip = -> Revolution003
FEATURE [PartDesign::Body] Body020  label="Handle up001"
  Group = -> [Sketch026,DatumPlane002,CopyBox002,Sketch024,AdditiveLoft006]
  Origin = -> Origin017
  Placement = pos=(0,0,-10) rot=(0,0,1;0rad)
  Tip = -> AdditiveLoft006
FEATURE [Sketcher::SketchObject] Sketch027
  AttachmentOffset = pos=(0,0,108) rot=(0,0,1;0rad)
  FullyConstrained = false
  MapMode = 5
  Placement = pos=(0,0,108) rot=(0,0,1;0rad)
  Support = -> [XY_Plane019]
  sketch-geometry (5):
    g0: LineSegment StartX=13.4509 StartY=2.99279 StartZ=0 EndX=13.4509 EndY=-2.99279 EndZ=0
    g1: LineSegment StartX=13.4509 StartY=2.99279 StartZ=0 EndX=14.5401 EndY=2.99279 EndZ=0
    g2: LineSegment StartX=13.4509 StartY=-2.99279 StartZ=0 EndX=14.5401 EndY=-2.99279 EndZ=0
    g3: ArcOfCircle CenterX=14.6831 CenterY=0 CenterZ=0 NormalX=0 NormalY=0 NormalZ=1 AngleXU=0 Radius=2.99621 StartAngle=4.66462 EndAngle=7.90175
    g4: LineSegment StartX=14.5401 StartY=2.99279 StartZ=0 EndX=14.5401 EndY=-2.99279 EndZ=0
  constraints (11):
    c: Vertical(g0)
    c: Coincident(g1,g0)
    c: Horizontal(g1)
    c: Coincident(g2,g0)
    c: Horizontal(g2)
    c: Coincident(g3,g1)
    c: Coincident(g3,g2)
    c: PointOnObject(g3,g-1)
    c: Coincident(g4,g1)
    c: Coincident(g4,g2)
    c: Vertical(g4)
FEATURE [PartDesign::Pad] Pad006
  Direction = (0,0,1)
  Length = 17
  Length2 = 10
  Profile = -> Sketch027
  ReferenceAxis = -> Sketch027 [N_Axis]
  Type = 0
FEATURE [PartDesign::Body] Body018
  Group = -> [Sketch027,Pad006]
  Origin = -> Origin020
  Tip = -> Pad006
FEATURE [Sketcher::SketchObject] Sketch028  label="Sketch down001"
  AttachmentOffset = pos=(0,0,134) rot=(0,0,1;0rad)
  FullyConstrained = false
  MapMode = 5
  Placement = pos=(0,0,134) rot=(0,0,1;0rad)
  Support = -> [XY_Plane020]
  sketch-geometry (11):
    g0: ArcOfCircle CenterX=0 CenterY=0 CenterZ=0 NormalX=0 NormalY=0 NormalZ=1 AngleXU=0 Radius=10.432 StartAngle=1.15238 EndAngle=5.13081
    g1: LineSegment StartX=4.2387 StartY=-9.53202 StartZ=0 EndX=4.2387 EndY=9.53202 EndZ=0
    g2: LineSegment StartX=13.0386 StartY=-5.6648 StartZ=0 EndX=4.2387 EndY=-9.53202 EndZ=0
    g3: LineSegment StartX=13.0386 StartY=5.61889 StartZ=0 EndX=4.2387 EndY=9.53202 EndZ=0
    g4: LineSegment StartX=14.8575 StartY=8.17194 StartZ=0 EndX=24.8171 EndY=8.17194 EndZ=0
    g5: LineSegment StartX=14.8575 StartY=-8.17194 StartZ=0 EndX=24.8171 EndY=-8.17194 EndZ=0
    g6: ArcOfCircle CenterX=20.7229 CenterY=0 CenterZ=0 NormalX=0 NormalY=0 NormalZ=1 AngleXU=0 Radius=9.14017 StartAngle=5.17684 EndAngle=7.38953
    g7: LineSegment StartX=13.0386 StartY=6.353 StartZ=0 EndX=13.0386 EndY=-6.353 EndZ=0
    g8: ArcOfCircle CenterX=14.8575 CenterY=6.353 CenterZ=0 NormalX=0 NormalY=0 NormalZ=1 AngleXU=0 Radius=1.81894 StartAngle=1.5708 EndAngle=3.14159
    g9: ArcOfCircle CenterX=14.8575 CenterY=-6.353 CenterZ=0 NormalX=0 NormalY=0 NormalZ=1 AngleXU=0 Radius=1.81894 StartAngle=3.14159 EndAngle=4.71239
    g10: LineSegment StartX=13.0386 StartY=-6.353 StartZ=0 EndX=13.0386 EndY=6.353 EndZ=0
  constraints (22):
    c: Coincident(g0,g-1)
    c: Coincident(g1,g0)
    c: Coincident(g1,g0)
    c: Vertical(g1)
    c: Coincident(g2,g0)
    c: Tangent(g3,g0) = -1.5708
    c: Horizontal(g4)
    c: Horizontal(g5)
    c: Equal(g4,g5)
    c: Coincident(g6,g4)
    c: Coincident(g6,g5)
    c: PointOnObject(g6,g-1)
    c: Vertical(g7)
    c: PointOnObject(g2,g7)
    c: PointOnObject(g3,g7)
    c: Tangent(g4,g8) = 1.5708
    c: Tangent(g7,g8) = -1.5708
    c: Tangent(g5,g9) = -1.5708
    c: Tangent(g7,g9) = -1.5708
    c: Equal(g9,g8)
    c: Coincident(g10,g9)
    c: Coincident(g10,g8)
FEATURE [Sketcher::SketchObject] Sketch029  label="Sketch up001"
  FullyConstrained = false
  MapMode = 5
  Placement = pos=(-2.20015,-22,145.841) rot=(0,1,0;0.261799rad)
  Support = -> [DatumPlane003]
  sketch-geometry (13):
    g0: ArcOfCircle CenterX=4.50884 CenterY=22 CenterZ=0 NormalX=0 NormalY=0 NormalZ=1 AngleXU=0 Radius=10.4954 StartAngle=1.10018 EndAngle=5.183
    g1: LineSegment StartX=4.50884 StartY=22 StartZ=0 EndX=41.871 EndY=22 EndZ=0
    g2: LineSegment StartX=15.8862 StartY=27.9874 StartZ=0 EndX=9.26778 EndY=31.3544 EndZ=0
    g3: LineSegment StartX=15.8862 StartY=15.9218 StartZ=0 EndX=9.26778 EndY=12.6456 EndZ=0
    g4: LineSegment StartX=9.26778 StartY=12.6456 StartZ=0 EndX=9.26778 EndY=31.3544 EndZ=0
    g5: LineSegment StartX=15.8862 StartY=27.9874 StartZ=0 EndX=15.8862 EndY=15.9218 EndZ=0
    g6: LineSegment StartX=17.5392 StartY=13.7739 StartZ=0 EndX=27.6466 EndY=13.7739 EndZ=0
    g7: LineSegment StartX=17.5392 StartY=30.2261 StartZ=0 EndX=27.6466 EndY=30.2261 EndZ=0
    g8: ArcOfCircle CenterX=23.8665 CenterY=22 CenterZ=0 NormalX=0 NormalY=0 NormalZ=1 AngleXU=0 Radius=9.05303 StartAngle=5.14314 EndAngle=7.42323
    g9: LineSegment StartX=15.8862 StartY=15.4269 StartZ=0 EndX=15.8862 EndY=28.5731 EndZ=0
    g10: ArcOfCircle CenterX=17.5392 CenterY=28.5731 CenterZ=0 NormalX=0 NormalY=0 NormalZ=1 AngleXU=0 Radius=1.65299 StartAngle=1.5708 EndAngle=3.14159
    g11: ArcOfCircle CenterX=17.5392 CenterY=15.4269 CenterZ=0 NormalX=0 NormalY=0 NormalZ=1 AngleXU=0 Radius=1.65299 StartAngle=3.14159 EndAngle=4.71239
    g12: LineSegment StartX=15.8862 StartY=15.4269 StartZ=0 EndX=15.8862 EndY=28.5731 EndZ=0
  constraints (26):
    c: DistanceY(g0) = 22
    c: Horizontal(g1)
    c: Coincident(g4,g3)
    c: Coincident(g4,g2)
    c: Vertical(g4)
    c: Coincident(g0,g3)
    c: Coincident(g1,g0)
    c: Vertical(g5)
    c: Tangent(g0,g2) = -1.5708
    c: Coincident(g5,g3)
    c: Coincident(g2,g5)
    c: Horizontal(g6)
    c: Horizontal(g7)
    c: Equal(g7,g6)
    c: Coincident(g8,g7)
    c: Coincident(g8,g6)
    c: PointOnObject(g8,g1)
    c: Vertical(g9)
    c: PointOnObject(g2,g9)
    c: Tangent(g7,g10) = 1.5708
    c: Tangent(g9,g10) = 1.5708
    c: Tangent(g6,g11) = -1.5708
    c: Tangent(g9,g11) = 1.5708
    c: Coincident(g12,g11)
    c: Coincident(g12,g10)
    c: Equal(g10,g11)
FEATURE [PartDesign::AdditiveLoft] AdditiveLoft007
  Closed = false
  Profile = -> Sketch028
  Ruled = false
  Sections = -> [Sketch029]
FEATURE [PartDesign::Body] Body017  label="Handle003"
  Group = -> [Sketch028,DatumPlane003,CopyBox003,Sketch029,AdditiveLoft007]
  Origin = -> Origin013
  Placement = pos=(0,0,-10) rot=(0,0,1;0rad)
  Tip = -> AdditiveLoft007
FEATURE [Part::Compound] Compound004  label="Tip disposal button001"
  Links = -> [Body018,Body017]
  Placement = pos=(0,0,-10) rot=(0,0,1;0rad)
FEATURE [Part::Compound] Compound005  label="Upper part001"
  Links = -> [Body014,Body020,Body019,Compound004,Body016,Body015]
FEATURE [TechDraw::DrawSVGTemplate] Template
  Height = 297
  Orientation = 1
  Width = 420
FEATURE [TechDraw::DrawViewPart] View001
  CoarseView = false
  Direction = (-0.43,-0.873,0.231)
  Focus = 100
  HardHidden = false
  IsoCount = 0
  IsoHidden = false
  IsoVisible = false
  LockPosition = false
  Perspective = false
  Rotation = 0
  ScaleType = 0
  SeamHidden = false
  SeamVisible = true
  SmoothHidden = false
  SmoothVisible = true
  Source = -> [Compound003]
  X = 77.7986
  XDirection = (0.899,-0.438,0.019)
  Y = 153.858
FEATURE [TechDraw::DrawViewPart] View003
  CoarseView = false
  Direction = (-0.43,-0.873,0.231)
  Focus = 100
  HardHidden = false
  IsoCount = 0
  IsoHidden = false
  IsoVisible = false
  LockPosition = false
  Perspective = false
  Rotation = 0
  Scale = 0.25
  ScaleType = 2
  SeamHidden = false
  SeamVisible = true
  SmoothHidden = false
  SmoothVisible = true
  Source = -> [Compound003]
  X = 261.436
  XDirection = (0.899,-0.438,0.019)
  Y = 173.265
FEATURE [Part::Thickness] Thickness003  label="2-200 tip002"
  Intersection = false
  Join = 0
  Mode = 0
  Placement = pos=(0,0,-137) rot=(0,0,1;0rad)
  SelfIntersection = false
  Value = 0.1
FEATURE [Image::ImagePlane] ImagePlane001
  Placement = pos=(12,0,10) rot=(-1,0,0;4.71239rad)
  XSize = 328.222
  YSize = 328.222
FEATURE [Sketcher::SketchObject] Sketch030
  FullyConstrained = false
  MapMode = 5
  Placement = pos=(0,0,0) rot=(1,0,0;1.5708rad)
  Support = -> [XZ_Plane023]
  sketch-geometry (4):
    g0: LineSegment StartX=0 StartY=-105.635 StartZ=0 EndX=1.73982 EndY=-105.635 EndZ=0
    g1: LineSegment StartX=1.73982 StartY=-105.635 StartZ=0 EndX=2.23827 EndY=-95.7656 EndZ=0
    g2: LineSegment StartX=2.23827 StartY=-95.7656 StartZ=0 EndX=0 EndY=-95.7656 EndZ=0
    g3: LineSegment StartX=0 StartY=-105.635 StartZ=0 EndX=0 EndY=-95.7656 EndZ=0
  constraints (8):
    c: PointOnObject(g0,g-2)
    c: Coincident(g1,g0)
    c: Coincident(g2,g1)
    c: PointOnObject(g2,g-2)
    c: Horizontal(g2)
    c: Coincident(g3,g0)
    c: Coincident(g3,g2)
    c: Horizontal(g0)
FEATURE [PartDesign::Revolution] Revolution006
  Angle = 360
  Axis = (0,2e-16,1)
  Base = (0,0,0)
  Placement = pos=(0,0,0) rot=(1,0,0;1.5708rad)
  Profile = -> Sketch030
  ReferenceAxis = -> Sketch030 [V_Axis]
  Reversed = true
FEATURE [PartDesign::Body] Body021  label="Tips holder"
  Group = -> [Revolution006,Sketch030]
  Origin = -> Origin021
  Placement = pos=(0,0,10) rot=(0,0,1;0rad)
  Tip = -> Revolution006
FEATURE [PartDesign::ShapeBinder] CopyBox004
  Placement = pos=(-11,-22,113) rot=(0,1,0;0.261799rad)
  TraceSupport = false
FEATURE [PartDesign::ShapeBinder] CopyBox005
  Placement = pos=(-11,-22,113) rot=(0,1,0;0.261799rad)
  TraceSupport = false
FEATURE [PartDesign::Plane] DatumPlane004
  AttachmentOffset = pos=(0,0,13) rot=(0,0,1;0rad)
  Length = 82.3639
  MapMode = 5
  Placement = pos=(-5.04716,-22,135.216) rot=(0,1,0;0.261799rad)
  ResizeMode = 0
  Support = -> [CopyBox004]
  Width = 61.8735
FEATURE [PartDesign::Plane] DatumPlane005
  AttachmentOffset = pos=(0,0,24) rot=(0,0,1;0rad)
  Length = 82.3639
  MapMode = 5
  Placement = pos=(-2.20015,-22,145.841) rot=(0,1,0;0.261799rad)
  ResizeMode = 0
  Support = -> [CopyBox005]
  Width = 61.8735
FEATURE [Sketcher::SketchObject] Sketch031
  AttachmentOffset = pos=(0,0,30) rot=(0,0,1;0rad)
  FullyConstrained = false
  MapMode = 5
  Placement = pos=(0,0,30) rot=(0,0,1;0rad)
  Support = -> [XY_Plane022]
  sketch-geometry (6):
    g0: ArcOfCircle CenterX=0 CenterY=0 CenterZ=0 NormalX=0 NormalY=0 NormalZ=1 AngleXU=0 Radius=10.5222 StartAngle=1.15093 EndAngle=5.13225
    g1: ArcOfCircle CenterX=13.606 CenterY=0 CenterZ=0 NormalX=0 NormalY=0 NormalZ=1 AngleXU=0 Radius=4.99301 StartAngle=5.04934 EndAngle=7.51703
    g2: LineSegment StartX=4.28922 StartY=-9.60826 StartZ=0 EndX=4.28922 EndY=9.60826 EndZ=0
    g3: LineSegment StartX=15.2568 StartY=4.71224 StartZ=0 EndX=4.28922 EndY=9.60826 EndZ=0
    g4: LineSegment StartX=15.2568 StartY=-4.71224 StartZ=0 EndX=4.28922 EndY=-9.60826 EndZ=0
    g5: LineSegment StartX=15.2568 StartY=-4.71224 StartZ=0 EndX=15.2568 EndY=4.71224 EndZ=0
  constraints (12):
    c: Coincident(g0,g-1)
    c: PointOnObject(g1,g-1)
    c: Coincident(g2,g0)
    c: Coincident(g2,g0)
    c: Vertical(g2)
    c: Coincident(g3,g1)
    c: Coincident(g3,g0)
    c: Coincident(g4,g1)
    c: Coincident(g4,g0)
    c: Coincident(g5,g1)
    c: Coincident(g5,g1)
    c: Vertical(g5)
FEATURE [PartDesign::Pad] Pad010
  Direction = (0,0,1)
  Length = 89
  Length2 = 10
  Profile = -> Sketch031
  ReferenceAxis = -> Sketch031 [N_Axis]
  Type = 0
FEATURE [PartDesign::Body] Body022  label="Handle down002"
  Group = -> [Sketch031,Pad010]
  Origin = -> Origin022
  Placement = pos=(0,0,-10) rot=(0,0,1;0rad)
  Tip = -> Pad010
FEATURE [Sketcher::SketchObject] Sketch032
  FullyConstrained = false
  MapMode = 5
  Placement = pos=(0,0,0) rot=(1,0,0;1.5708rad)
  Support = -> [XZ_Plane026]
  sketch-geometry (13):
    g0: LineSegment StartX=0 StartY=126.907 StartZ=0 EndX=4.00392 EndY=126.907 EndZ=0
    g1: LineSegment StartX=4.00392 StartY=126.907 StartZ=0 EndX=4.00392 EndY=149.155 EndZ=0
    g2: LineSegment StartX=4.00392 StartY=149.155 StartZ=0 EndX=6.1092 EndY=149.155 EndZ=0
    g3: LineSegment StartX=6.1092 StartY=149.155 StartZ=0 EndX=7.56082 EndY=151.528 EndZ=0
    g4: LineSegment StartX=6.45502 StartY=156.073 StartZ=0 EndX=5.512 EndY=156.456 EndZ=0
    g5: LineSegment StartX=5.13623 StartY=156.529 StartZ=0 EndX=0 EndY=156.529 EndZ=0
    g6: ArcOfCircle CenterX=3.32106 CenterY=152.491 CenterZ=0 NormalX=0 NormalY=0 NormalZ=1 AngleXU=0 Radius=4.34777 StartAngle=5.40856 EndAngle=6.05983
    g7: LineSegment StartX=7.56082 StartY=151.528 StartZ=0 EndX=7.56082 EndY=152.922 EndZ=0
    g8: LineSegment StartX=6.79086 StartY=155.718 StartZ=0 EndX=7.38546 EndY=153.978 EndZ=0
    g9: ArcOfCircle CenterX=4.2961 CenterY=152.922 CenterZ=0 NormalX=0 NormalY=0 NormalZ=1 AngleXU=0 Radius=3.26472 StartAngle=0 EndAngle=0.329246
    g10: ArcOfCircle CenterX=6.23382 CenterY=155.528 CenterZ=0 NormalX=0 NormalY=0 NormalZ=1 AngleXU=0 Radius=0.588658 StartAngle=0.329246 EndAngle=1.18556
    g11: ArcOfCircle CenterX=5.13623 CenterY=155.529 CenterZ=0 NormalX=0 NormalY=0 NormalZ=1 AngleXU=0 Radius=1 StartAngle=1.18556 EndAngle=1.5708
    g12: LineSegment StartX=0 StartY=156.529 StartZ=0 EndX=0 EndY=126.907 EndZ=0
  constraints (22):
    c: PointOnObject(g0,g-2)
    c: Horizontal(g0)
    c: Coincident(g1,g0)
    c: Vertical(g1)
    c: Coincident(g2,g1)
    c: Horizontal(g2)
    c: Coincident(g3,g2)
    c: Horizontal(g5)
    c: Coincident(g6,g2)
    c: Coincident(g6,g3)
    c: Coincident(g7,g6)
    c: Vertical(g7)
    c: Tangent(g7,g9) = -1.5708
    c: Tangent(g8,g9) = 1.5708
    c: Tangent(g8,g10) = 1.5708
    c: Tangent(g4,g10) = -1.5708
    c: Tangent(g4,g11) = -1.5708
    c: Tangent(g5,g11) = -1.5708
    c: Coincident(g12,g5)
    c: Coincident(g12,g0)
    c: Vertical(g12)
    c: Radius(g11) = 1
FEATURE [PartDesign::Revolution] Revolution007
  Angle = 360
  Axis = (0,2e-16,1)
  Base = (0,0,0)
  Placement = pos=(0,0,0) rot=(1,0,0;1.5708rad)
  Profile = -> Sketch032
  ReferenceAxis = -> Sketch032 [V_Axis]
  Reversed = true
FEATURE [PartDesign::Body] Body023  label="Button002"
  Group = -> [Sketch032,Revolution007]
  Origin = -> Origin023
  Placement = pos=(0,0,-13) rot=(0,0,1;0rad)
  Tip = -> Revolution007
FEATURE [Sketcher::SketchObject] Sketch033
  AttachmentOffset = pos=(0,0,119) rot=(0,0,1;0rad)
  FullyConstrained = false
  MapMode = 5
  Placement = pos=(0,0,119) rot=(0,0,1;0rad)
  Support = -> [XY_Plane024]
  sketch-geometry (5):
    g0: ArcOfCircle CenterX=0 CenterY=0 CenterZ=0 NormalX=0 NormalY=0 NormalZ=1 AngleXU=0 Radius=10.5554 StartAngle=1.15011 EndAngle=5.13308
    g1: LineSegment StartX=4.31068 StartY=-9.63502 StartZ=0 EndX=4.31068 EndY=9.63502 EndZ=0
    g2: LineSegment StartX=12.3594 StartY=6.03403 StartZ=0 EndX=12.3594 EndY=-5.98739 EndZ=0
    g3: LineSegment StartX=12.3594 StartY=-5.98739 StartZ=0 EndX=4.31068 EndY=-9.63502 EndZ=0
    g4: LineSegment StartX=12.3594 StartY=6.03403 StartZ=0 EndX=4.31068 EndY=9.63502 EndZ=0
  constraints (9):
    c: Coincident(g0,g-1)
    c: Coincident(g1,g0)
    c: Coincident(g1,g0)
    c: Vertical(g1)
    c: Vertical(g2)
    c: Coincident(g3,g2)
    c: Coincident(g3,g0)
    c: Coincident(g4,g2)
    c: Tangent(g4,g0) = -1.5708
FEATURE [Sketcher::SketchObject] Sketch034
  FullyConstrained = false
  MapMode = 5
  Placement = pos=(-5.04716,-22,135.216) rot=(0,1,0;0.261799rad)
  Support = -> [DatumPlane004]
  sketch-geometry (6):
    g0: ArcOfCircle CenterX=4.89643 CenterY=22 CenterZ=0 NormalX=0 NormalY=0 NormalZ=1 AngleXU=0 Radius=10.6127 StartAngle=1.17267 EndAngle=5.11052
    g1: LineSegment StartX=4.89643 StartY=22 StartZ=0 EndX=41.871 EndY=22 EndZ=0
    g2: LineSegment StartX=18.1252 StartY=27.9493 StartZ=0 EndX=9.01089 EndY=31.7827 EndZ=0
    g3: LineSegment StartX=18.1252 StartY=15.9745 StartZ=0 EndX=9.01089 EndY=12.2173 EndZ=0
    g4: LineSegment StartX=9.01089 StartY=12.2173 StartZ=0 EndX=9.01089 EndY=31.7827 EndZ=0
    g5: LineSegment StartX=18.1252 StartY=27.9493 StartZ=0 EndX=18.1252 EndY=15.9745 EndZ=0
  constraints (11):
    c: DistanceY(g0) = 22
    c: Horizontal(g1)
    c: Coincident(g4,g3)
    c: Coincident(g4,g2)
    c: Vertical(g4)
    c: Coincident(g0,g3)
    c: Coincident(g1,g0)
    c: Vertical(g5)
    c: Tangent(g0,g2) = -1.5708
    c: Coincident(g5,g3)
    c: Coincident(g2,g5)
FEATURE [PartDesign::AdditiveLoft] AdditiveLoft008
  Closed = false
  Profile = -> Sketch033
  Ruled = false
  Sections = -> [Sketch034]
FEATURE [PartDesign::Body] Body024  label="Handle up002"
  Group = -> [Sketch033,DatumPlane004,CopyBox004,Sketch034,AdditiveLoft008]
  Origin = -> Origin024
  Placement = pos=(0,0,-10) rot=(0,0,1;0rad)
  Tip = -> AdditiveLoft008
FEATURE [Sketcher::SketchObject] Sketch035
  FullyConstrained = false
  MapMode = 5
  Placement = pos=(0,0,0) rot=(1,0,0;1.5708rad)
  Support = -> [XZ_Plane028]
  sketch-geometry (12):
    g0: LineSegment StartX=-6.06998 StartY=126.439 StartZ=0 EndX=-32.1503 EndY=115.111 EndZ=0
    g1: LineSegment StartX=-9.74812 StartY=110.531 StartZ=0 EndX=-9.74812 EndY=125.946 EndZ=0
    g2: LineSegment StartX=-9.74812 StartY=125.946 StartZ=0 EndX=-5.84974 EndY=125.946 EndZ=0
    g3: LineSegment StartX=-9.74812 StartY=110.531 StartZ=0 EndX=-5.84974 EndY=110.531 EndZ=0
    g4: ArcOfCircle CenterX=-20.1675 CenterY=112.928 CenterZ=0 NormalX=0 NormalY=0 NormalZ=1 AngleXU=0 Radius=12.18 StartAngle=0.544381 EndAngle=2.96141
    g5: ArcOfCircle CenterX=-20.139 CenterY=117.805 CenterZ=0 NormalX=0 NormalY=0 NormalZ=1 AngleXU=0 Radius=13.2 StartAngle=0.66456 EndAngle=3.34717
    g6: LineSegment StartX=-9.74812 StartY=119.236 StartZ=0 EndX=-9.74812 EndY=110.531 EndZ=0
    g7: LineSegment StartX=-6.06998 StartY=110.648 StartZ=0 EndX=-9.74812 EndY=110.531 EndZ=0
    g8: LineSegment StartX=-6.06998 StartY=126.439 StartZ=0 EndX=-6.06998 EndY=110.648 EndZ=0
    g9: ArcOfCircle CenterX=-23.8722 CenterY=113.32 CenterZ=0 NormalX=0 NormalY=0 NormalZ=1 AngleXU=0 Radius=18.9448 StartAngle=0.349079 EndAngle=0.729456
    g10: LineSegment StartX=-6.06998 StartY=110.648 StartZ=0 EndX=-6.06998 EndY=119.799 EndZ=0
    g11: LineSegment StartX=-32.1503 StartY=115.111 StartZ=0 EndX=-33.0611 EndY=115.111 EndZ=0
  constraints (24):
    c: Vertical(g1)
    c: Coincident(g2,g1)
    c: Horizontal(g2)
    c: Coincident(g3,g1)
    c: Horizontal(g3)
    c: PointOnObject(g4,g1)
    c: Coincident(g4,g0)
    c: Coincident(g5,g1)
    c: Coincident(g6,g4)
    c: Coincident(g6,g1)
    c: Coincident(g7,g6)
    c: Radius(g5) = 13.2
    c: Radius(g4) = 12.18
    c: DistanceY(g4,g5) = 6.71
    c: Coincident(g8,g0)
    c: Coincident(g8,g7)
    c: Vertical(g8)
    c: Coincident(g9,g5)
    c: PointOnObject(g9,g8)
    c: Coincident(g10,g7)
    c: Coincident(g10,g9)
    c: Coincident(g11,g4)
    c: Coincident(g11,g5)
    c: Horizontal(g11)
FEATURE [PartDesign::Pad] Pad011
  Direction = (0,-1,2e-16)
  Length = 10
  Length2 = 10
  Midplane = true
  Placement = pos=(0,0,0) rot=(1,0,0;1.5708rad)
  Profile = -> Sketch035
  ReferenceAxis = -> Sketch035 [N_Axis]
  Type = 0
FEATURE [PartDesign::Body] Body025  label="Hook002"
  Group = -> [Sketch035,Pad011]
  Origin = -> Origin025
  Tip = -> Pad011
FEATURE [Sketcher::SketchObject] Sketch036  label="Sketch up002"
  FullyConstrained = false
  MapMode = 5
  Placement = pos=(-2.20015,-22,145.841) rot=(0,1,0;0.261799rad)
  Support = -> [DatumPlane005]
  sketch-geometry (13):
    g0: ArcOfCircle CenterX=4.50884 CenterY=22 CenterZ=0 NormalX=0 NormalY=0 NormalZ=1 AngleXU=0 Radius=10.4954 StartAngle=1.10018 EndAngle=5.183
    g1: LineSegment StartX=4.50884 StartY=22 StartZ=0 EndX=41.871 EndY=22 EndZ=0
    g2: LineSegment StartX=15.8862 StartY=27.9874 StartZ=0 EndX=9.26778 EndY=31.3544 EndZ=0
    g3: LineSegment StartX=15.8862 StartY=15.9218 StartZ=0 EndX=9.26778 EndY=12.6456 EndZ=0
    g4: LineSegment StartX=9.26778 StartY=12.6456 StartZ=0 EndX=9.26778 EndY=31.3544 EndZ=0
    g5: LineSegment StartX=15.8862 StartY=27.9874 StartZ=0 EndX=15.8862 EndY=15.9218 EndZ=0
    g6: LineSegment StartX=17.5392 StartY=13.7739 StartZ=0 EndX=27.6466 EndY=13.7739 EndZ=0
    g7: LineSegment StartX=17.5392 StartY=30.2261 StartZ=0 EndX=27.6466 EndY=30.2261 EndZ=0
    g8: ArcOfCircle CenterX=23.8665 CenterY=22 CenterZ=0 NormalX=0 NormalY=0 NormalZ=1 AngleXU=0 Radius=9.05303 StartAngle=5.14314 EndAngle=7.42323
    g9: LineSegment StartX=15.8862 StartY=15.4269 StartZ=0 EndX=15.8862 EndY=28.5731 EndZ=0
    g10: ArcOfCircle CenterX=17.5392 CenterY=28.5731 CenterZ=0 NormalX=0 NormalY=0 NormalZ=1 AngleXU=0 Radius=1.65299 StartAngle=1.5708 EndAngle=3.14159
    g11: ArcOfCircle CenterX=17.5392 CenterY=15.4269 CenterZ=0 NormalX=0 NormalY=0 NormalZ=1 AngleXU=0 Radius=1.65299 StartAngle=3.14159 EndAngle=4.71239
    g12: LineSegment StartX=15.8862 StartY=15.4269 StartZ=0 EndX=15.8862 EndY=28.5731 EndZ=0
  constraints (26):
    c: DistanceY(g0) = 22
    c: Horizontal(g1)
    c: Coincident(g4,g3)
    c: Coincident(g4,g2)
    c: Vertical(g4)
    c: Coincident(g0,g3)
    c: Coincident(g1,g0)
    c: Vertical(g5)
    c: Tangent(g0,g2) = -1.5708
    c: Coincident(g5,g3)
    c: Coincident(g2,g5)
    c: Horizontal(g6)
    c: Horizontal(g7)
    c: Equal(g7,g6)
    c: Coincident(g8,g7)
    c: Coincident(g8,g6)
    c: PointOnObject(g8,g1)
    c: Vertical(g9)
    c: PointOnObject(g2,g9)
    c: Tangent(g7,g10) = 1.5708
    c: Tangent(g9,g10) = 1.5708
    c: Tangent(g6,g11) = -1.5708
    c: Tangent(g9,g11) = 1.5708
    c: Coincident(g12,g11)
    c: Coincident(g12,g10)
    c: Equal(g10,g11)
FEATURE [Sketcher::SketchObject] Sketch037  label="Sketch down002"
  AttachmentOffset = pos=(0,0,134) rot=(0,0,1;0rad)
  FullyConstrained = false
  MapMode = 5
  Placement = pos=(0,0,134) rot=(0,0,1;0rad)
  Support = -> [XY_Plane026]
  sketch-geometry (11):
    g0: ArcOfCircle CenterX=0 CenterY=0 CenterZ=0 NormalX=0 NormalY=0 NormalZ=1 AngleXU=0 Radius=10.432 StartAngle=1.15238 EndAngle=5.13081
    g1: LineSegment StartX=4.2387 StartY=-9.53202 StartZ=0 EndX=4.2387 EndY=9.53202 EndZ=0
    g2: LineSegment StartX=13.0386 StartY=-5.6648 StartZ=0 EndX=4.2387 EndY=-9.53202 EndZ=0
    g3: LineSegment StartX=13.0386 StartY=5.61889 StartZ=0 EndX=4.2387 EndY=9.53202 EndZ=0
    g4: LineSegment StartX=14.8575 StartY=8.17194 StartZ=0 EndX=24.8171 EndY=8.17194 EndZ=0
    g5: LineSegment StartX=14.8575 StartY=-8.17194 StartZ=0 EndX=24.8171 EndY=-8.17194 EndZ=0
    g6: ArcOfCircle CenterX=20.7229 CenterY=0 CenterZ=0 NormalX=0 NormalY=0 NormalZ=1 AngleXU=0 Radius=9.14017 StartAngle=5.17684 EndAngle=7.38953
    g7: LineSegment StartX=13.0386 StartY=6.353 StartZ=0 EndX=13.0386 EndY=-6.353 EndZ=0
    g8: ArcOfCircle CenterX=14.8575 CenterY=6.353 CenterZ=0 NormalX=0 NormalY=0 NormalZ=1 AngleXU=0 Radius=1.81894 StartAngle=1.5708 EndAngle=3.14159
    g9: ArcOfCircle CenterX=14.8575 CenterY=-6.353 CenterZ=0 NormalX=0 NormalY=0 NormalZ=1 AngleXU=0 Radius=1.81894 StartAngle=3.14159 EndAngle=4.71239
    g10: LineSegment StartX=13.0386 StartY=-6.353 StartZ=0 EndX=13.0386 EndY=6.353 EndZ=0
  constraints (22):
    c: Coincident(g0,g-1)
    c: Coincident(g1,g0)
    c: Coincident(g1,g0)
    c: Vertical(g1)
    c: Coincident(g2,g0)
    c: Tangent(g3,g0) = -1.5708
    c: Horizontal(g4)
    c: Horizontal(g5)
    c: Equal(g4,g5)
    c: Coincident(g6,g4)
    c: Coincident(g6,g5)
    c: PointOnObject(g6,g-1)
    c: Vertical(g7)
    c: PointOnObject(g2,g7)
    c: PointOnObject(g3,g7)
    c: Tangent(g4,g8) = 1.5708
    c: Tangent(g7,g8) = -1.5708
    c: Tangent(g5,g9) = -1.5708
    c: Tangent(g7,g9) = -1.5708
    c: Equal(g9,g8)
    c: Coincident(g10,g9)
    c: Coincident(g10,g8)
FEATURE [PartDesign::AdditiveLoft] AdditiveLoft009
  Closed = false
  Profile = -> Sketch037
  Ruled = false
  Sections = -> [Sketch036]
FEATURE [PartDesign::Body] Body026  label="Handle004"
  Group = -> [Sketch037,DatumPlane005,CopyBox005,Sketch036,AdditiveLoft009]
  Origin = -> Origin026
  Placement = pos=(0,0,-10) rot=(0,0,1;0rad)
  Tip = -> AdditiveLoft009
FEATURE [Sketcher::SketchObject] Sketch038
  AttachmentOffset = pos=(0,0,108) rot=(0,0,1;0rad)
  FullyConstrained = false
  MapMode = 5
  Placement = pos=(0,0,108) rot=(0,0,1;0rad)
  Support = -> [XY_Plane027]
  sketch-geometry (5):
    g0: LineSegment StartX=13.4509 StartY=2.99279 StartZ=0 EndX=13.4509 EndY=-2.99279 EndZ=0
    g1: LineSegment StartX=13.4509 StartY=2.99279 StartZ=0 EndX=14.5401 EndY=2.99279 EndZ=0
    g2: LineSegment StartX=13.4509 StartY=-2.99279 StartZ=0 EndX=14.5401 EndY=-2.99279 EndZ=0
    g3: ArcOfCircle CenterX=14.6831 CenterY=0 CenterZ=0 NormalX=0 NormalY=0 NormalZ=1 AngleXU=0 Radius=2.99621 StartAngle=4.66462 EndAngle=7.90175
    g4: LineSegment StartX=14.5401 StartY=2.99279 StartZ=0 EndX=14.5401 EndY=-2.99279 EndZ=0
  constraints (11):
    c: Vertical(g0)
    c: Coincident(g1,g0)
    c: Horizontal(g1)
    c: Coincident(g2,g0)
    c: Horizontal(g2)
    c: Coincident(g3,g1)
    c: Coincident(g3,g2)
    c: PointOnObject(g3,g-1)
    c: Coincident(g4,g1)
    c: Coincident(g4,g2)
    c: Vertical(g4)
FEATURE [PartDesign::Pad] Pad012
  Direction = (0,0,1)
  Length = 17
  Length2 = 10
  Profile = -> Sketch038
  ReferenceAxis = -> Sketch038 [N_Axis]
  Type = 0
FEATURE [PartDesign::Body] Body027
  Group = -> [Sketch038,Pad012]
  Origin = -> Origin027
  Tip = -> Pad012
FEATURE [Part::Compound] Compound008  label="Tip disposal button002"
  Links = -> [Body027,Body026]
  Placement = pos=(0,0,-10) rot=(0,0,1;0rad)
FEATURE [Part::Compound] Compound009  label="Single channel Up"
  Links = -> [Compound008,Body022,Body023,Body024,Body025]
FEATURE [Sketcher::SketchObject] Sketch039
  FullyConstrained = false
  MapMode = 5
  Placement = pos=(0,0,0) rot=(1,0,0;1.5708rad)
  Support = -> [XZ_Plane031]
  sketch-geometry (4):
    g0: LineSegment StartX=0 StartY=-86.1555 StartZ=0 EndX=2.8048 EndY=-86.1555 EndZ=0
    g1: LineSegment StartX=2.8048 StartY=-86.1555 StartZ=0 EndX=4.9621 EndY=19.3897 EndZ=0
    g2: LineSegment StartX=4.9621 StartY=19.3897 StartZ=0 EndX=0 EndY=19.3897 EndZ=0
    g3: LineSegment StartX=0 StartY=19.3897 StartZ=0 EndX=0 EndY=-86.1555 EndZ=0
  constraints (8):
    c: PointOnObject(g0,g-2)
    c: Horizontal(g0)
    c: Coincident(g1,g0)
    c: Coincident(g2,g1)
    c: Horizontal(g2)
    c: Coincident(g3,g2)
    c: Coincident(g3,g0)
    c: Vertical(g3)
FEATURE [PartDesign::Revolution] Revolution008
  Angle = 360
  Axis = (0,2e-16,1)
  Base = (0,0,0)
  Placement = pos=(0,0,0) rot=(1,0,0;1.5708rad)
  Profile = -> Sketch039
  ReferenceAxis = -> Sketch039 [V_Axis]
  Reversed = true
FEATURE [PartDesign::Body] Body028  label="Single channel channel"
  Group = -> [Sketch039,Revolution008]
  Origin = -> Origin028
  Tip = -> Revolution008
FEATURE [Sketcher::SketchObject] Sketch040
  FullyConstrained = false
  MapMode = 5
  Support = -> [XY_Plane029]
  sketch-geometry (7):
    g0: LineSegment StartX=3.74831 StartY=7.81274 StartZ=0 EndX=13.7466 EndY=2.8718 EndZ=0
    g1: LineSegment StartX=3.74831 StartY=-7.81274 StartZ=0 EndX=13.7466 EndY=-2.8718 EndZ=0
    g2: LineSegment StartX=13.7466 StartY=-2.8718 StartZ=0 EndX=13.7466 EndY=0 EndZ=0
    g3: LineSegment StartX=13.7466 StartY=0 StartZ=0 EndX=13.7466 EndY=2.8718 EndZ=0
    g4: ArcOfCircle CenterX=12.3274 CenterY=0 CenterZ=0 NormalX=0 NormalY=0 NormalZ=1 AngleXU=0 Radius=3.20332 StartAngle=5.17137 EndAngle=7.395
    g5: ArcOfCircle CenterX=-0.112572 CenterY=8e-16 CenterZ=0 NormalX=0 NormalY=0 NormalZ=1 AngleXU=0 Radius=8.71466 StartAngle=1.11182 EndAngle=5.17137
    g6: LineSegment StartX=3.74831 StartY=-7.81274 StartZ=0 EndX=3.74831 EndY=7.81274 EndZ=0
  constraints (14):
    c: Coincident(g2,g1)
    c: PointOnObject(g2,g-1)
    c: Vertical(g2)
    c: Coincident(g3,g2)
    c: Coincident(g3,g0)
    c: Vertical(g3)
    c: PointOnObject(g4,g-1)
    c: Tangent(g4,g0) = 1.5708
    c: Tangent(g4,g1) = -1.5708
    c: Coincident(g5,g1)
    c: Tangent(g5,g0) = 1.5708
    c: Coincident(g6,g1)
    c: Coincident(g6,g0)
    c: Vertical(g6)
FEATURE [Sketcher::SketchObject] Sketch022
  FullyConstrained = false
  MapMode = 5
  Placement = pos=(0,0,0) rot=(1,0,0;1.5708rad)
  Support = -> [XZ_Plane034]
  sketch-geometry (4):
    g0: LineSegment StartX=0 StartY=-105.635 StartZ=0 EndX=1.73982 EndY=-105.635 EndZ=0
    g1: LineSegment StartX=1.73982 StartY=-105.635 StartZ=0 EndX=2.23827 EndY=-95.7656 EndZ=0
    g2: LineSegment StartX=2.23827 StartY=-95.7656 StartZ=0 EndX=0 EndY=-95.7656 EndZ=0
    g3: LineSegment StartX=0 StartY=-105.635 StartZ=0 EndX=0 EndY=-95.7656 EndZ=0
  constraints (8):
    c: PointOnObject(g0,g-2)
    c: Coincident(g1,g0)
    c: Coincident(g2,g1)
    c: PointOnObject(g2,g-2)
    c: Horizontal(g2)
    c: Coincident(g3,g0)
    c: Coincident(g3,g2)
    c: Horizontal(g0)
FEATURE [PartDesign::Revolution] Revolution004
  Angle = 360
  Axis = (0,2e-16,1)
  Base = (0,0,0)
  Placement = pos=(0,0,0) rot=(1,0,0;1.5708rad)
  Profile = -> Sketch022
  ReferenceAxis = -> Sketch022 [V_Axis]
  Reversed = true
FEATURE [PartDesign::Body] Revolution004Body
  Group = -> [Sketch022,Revolution004]
  Origin = -> Origin031
  Tip = -> Revolution004
FEATURE [Part::FeaturePython] Array010  label="Tips holders001"  # Draft array (typed FeaturePython)
  AlwaysSyncPlacement = false
  Angle = 360
  ArrayType = 0
  Axis = (0,0,1)
  Base = -> Revolution004Body
  Center = (0,0,0)
  Count = 8
  ExpandArray = false
  Fuse = false
  IntervalAxis = (0,0,0)
  IntervalX = (8.5,0,0)
  IntervalY = (0,100,0)
  IntervalZ = (0,0,100)
  NumberCircles = 3
  NumberPolar = 5
  NumberX = 8
  NumberY = 1
  NumberZ = 1
  Placement = pos=(-29.9,0,0) rot=(0,0,1;0rad)
  PlacementList = 8 placements: arithmetic series from (0,0,0) step (8.5,0,0) to (59.5,0,0)
  RadialDistance = 50
  ScaleList = (8) [(1,1,1),(1,1,1),(1,1,1),(1,1,1),(1,1,1),(1,1,1),(1,1,1),(1,1,1)]
  Symmetry = 1
  TangentialDistance = 25
FEATURE [Part::Compound] Compound006  label="Bottom part wo tips"
  Links = -> [Fillet001,Body013,Array010]
  Placement = pos=(0,0,0) rot=(0,0,1;1.5708rad)
FEATURE [Part::Compound] Compound007  label="200 multichannel wo tips"
  Links = -> [Compound006,Compound005]
  Placement = pos=(0,0,0) rot=(0,1,0;0.261799rad)
FEATURE [TechDraw::DrawViewPart] View
  CoarseView = false
  Direction = (-0.43,-0.873,0.231)
  Focus = 100
  HardHidden = false
  IsoCount = 0
  IsoHidden = false
  IsoVisible = false
  LockPosition = false
  Perspective = false
  Rotation = 0
  ScaleType = 0
  SeamHidden = false
  SeamVisible = true
  SmoothHidden = false
  SmoothVisible = true
  Source = -> [Compound007]
  X = 184.282
  XDirection = (0.899,-0.438,0.019)
  Y = 155.168
FEATURE [TechDraw::DrawViewPart] View002
  CoarseView = false
  Direction = (-0.43,-0.873,0.231)
  Focus = 100
  HardHidden = false
  IsoCount = 0
  IsoHidden = false
  IsoVisible = false
  LockPosition = false
  Perspective = false
  Rotation = 0
  Scale = 0.25
  ScaleType = 2
  SeamHidden = false
  SeamVisible = true
  SmoothHidden = false
  SmoothVisible = true
  Source = -> [Compound007]
  X = 269.056
  XDirection = (0.899,-0.438,0.019)
  Y = 255.182
FEATURE [TechDraw::DrawViewPart] View004
  CoarseView = false
  Direction = (-0.966,0,0.259)
  Focus = 100
  HardHidden = false
  IsoCount = 0
  IsoHidden = false
  IsoVisible = false
  LockPosition = false
  Perspective = false
  Rotation = 0
  ScaleType = 0
  SeamHidden = false
  SeamVisible = true
  SmoothHidden = false
  SmoothVisible = true
  Source = -> [Compound007]
  X = 352.401
  XDirection = (0,-0.966,0)
  Y = 150.405
FEATURE [TechDraw::DrawPage] Page
  KeepUpdated = true
  NextBalloonIndex = 1
  ProjectionType = 0
  Template = -> Template
  Views = -> [View,View001,View002,View003,View004]
FEATURE [App::Part] Part
  Group = -> [Revolution004Body]
  Origin = -> Origin030
FEATURE [PartDesign::Pad] Pad013
  Direction = (0,0,1)
  Length = 22
  Length2 = 10
  Profile = -> Sketch040
  ReferenceAxis = -> Sketch040 [N_Axis]
  Type = 0
FEATURE [PartDesign::Body] Body029  label="Single channel down"
  Group = -> [Sketch040,Pad013]
  Origin = -> Origin029
  Tip = -> Pad013
FEATURE [Part::Compound] Compound010  label="Single channel bottom"
  Links = -> [Body029,Body028,Body021]
FEATURE [Part::Compound] Compound011  label="Single channel"
  Links = -> [Compound010,Compound009]
  Placement = pos=(0,0,0) rot=(0,0,1;1.5708rad)
FEATURE [Part::FeaturePython] Clone  label="Single channel001"  # Draft clone (typed FeaturePython)
  AttacherType = Attacher::AttachEngine3D
  Fuse = false
  Objects = -> [Compound011]
  Scale = (1,1,1)
FEATURE [Part::Compound] Compound012  label="Single channel w tip"
  Links = -> [Thickness003,Clone]
  Placement = pos=(0,0,0) rot=(0,0,1;1.5708rad)
FEATURE [TechDraw::DrawSVGTemplate] Template001
  Height = 297
  Orientation = 1
  Width = 420
FEATURE [TechDraw::DrawViewPart] View005
  CoarseView = false
  Direction = (0.781,-0.618,0.095)
  Focus = 100
  HardHidden = false
  IsoCount = 0
  IsoHidden = false
  IsoVisible = false
  LockPosition = false
  Perspective = false
  Rotation = 0
  ScaleType = 0
  SeamHidden = false
  SeamVisible = true
  SmoothHidden = false
  SmoothVisible = true
  Source = -> [Compound011]
  X = 75.9055
  XDirection = (0.587,0.777,0.229)
  Y = 161.553
FEATURE [TechDraw::DrawViewPart] View006
  CoarseView = false
  Direction = (0.781,-0.618,0.095)
  Focus = 100
  HardHidden = false
  IsoCount = 0
  IsoHidden = false
  IsoVisible = false
  LockPosition = false
  Perspective = false
  Rotation = 0
  ScaleType = 0
  SeamHidden = false
  SeamVisible = true
  SmoothHidden = false
  SmoothVisible = true
  Source = -> [Compound012]
  X = 210
  XDirection = (0.587,0.777,0.229)
  Y = 148.5
FEATURE [TechDraw::DrawPage] Page001
  KeepUpdated = true
  NextBalloonIndex = 1
  ProjectionType = 0
  Template = -> Template001
  Views = -> [View005,View006]
